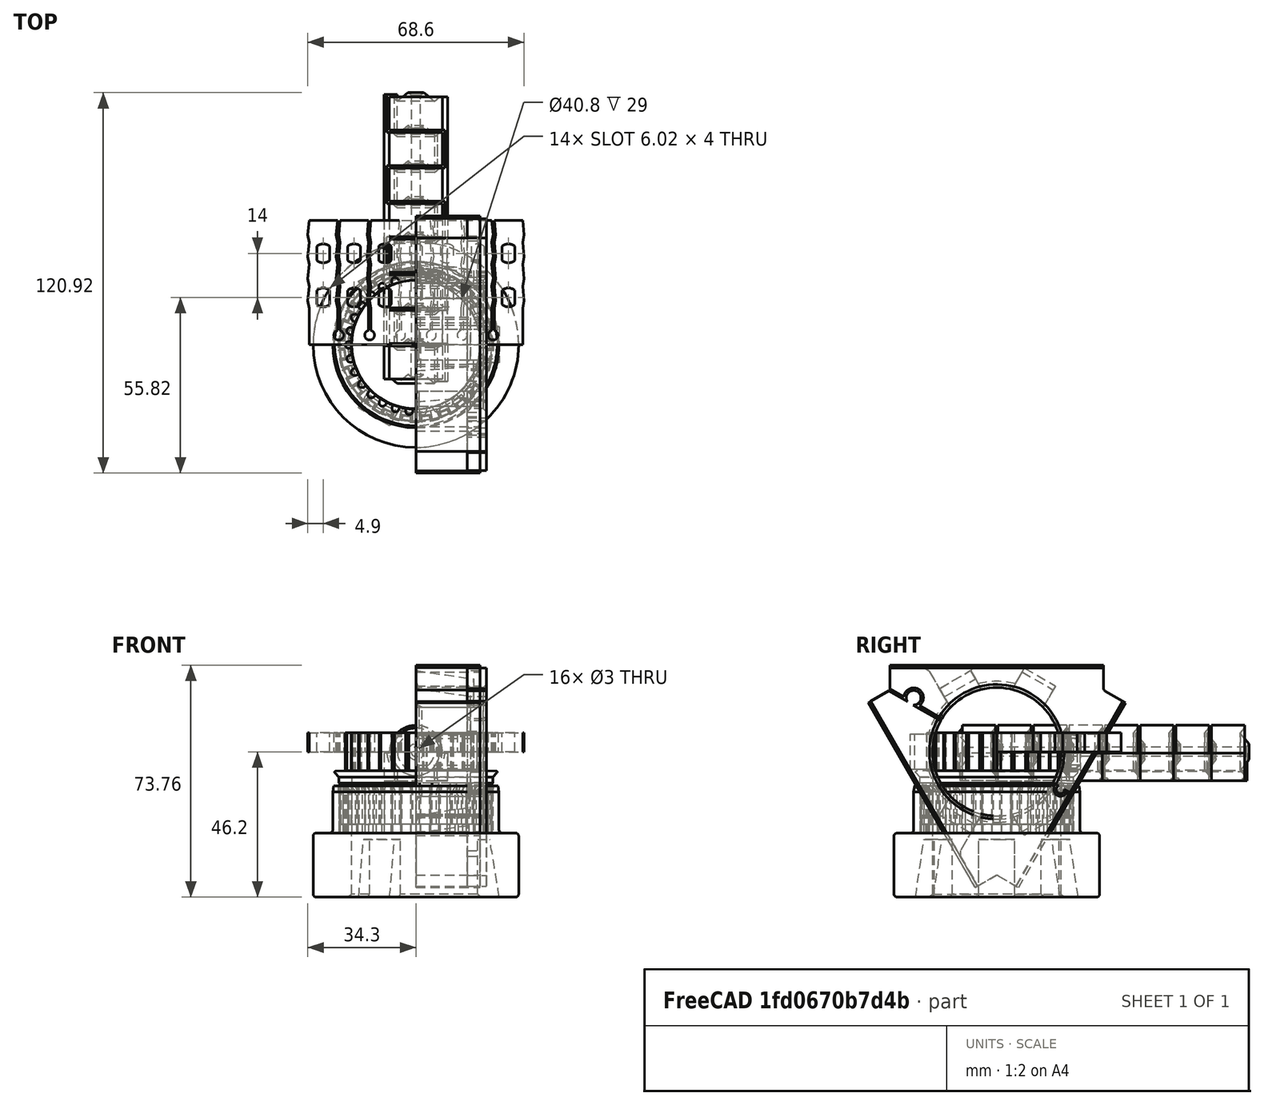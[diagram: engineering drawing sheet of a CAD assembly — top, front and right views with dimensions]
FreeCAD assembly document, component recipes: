
FREECAD ASSEMBLY — COMPONENT RECIPES ("BaseHingeModel_ver1.2_PulleOnAxis")

This assembly document has 9 components, labeled P0..P8 below (a component is one placed body or linked part). 9 of them carry a construction recipe — the FreeCAD feature program that regenerates the part from scratch, quoted from this document or its linked companion documents; the rest are supplied as boundary geometry only. No exploded tour is included for this assembly.
COMPONENT P0 — recipe-attached ("BeamFixatoPart", modeled in this document).
Construction recipe (the document's own serialized feature program — sketch geometry with constraints, then the solid features built on it; lengths are millimeters unless a unit is written):

FEATURE [Sketcher::SketchObject] Sketch022  label="FixatorBodySketch"
  FullyConstrained = false
  MapMode = 5
  Support = -> [XY_Plane005]
  expr: Constraints[143] = Spreadsheet.mmCellWall
  expr: Constraints[144] = Spreadsheet.mmCellWall
  expr: Constraints[145] = Spreadsheet.mmCellWall
  expr: Constraints[146] = Spreadsheet.mmCellWidth
  expr: Constraints[147] = Spreadsheet.mmCellWidth
  expr: Constraints[148] = Spreadsheet.mmCellWidth
  expr: Constraints[169] = Spreadsheet.mmCommonBaseLenght
  expr: Constraints[170] = Spreadsheet.mmToothStep
  expr: Constraints[171] = Spreadsheet.mmToothStep
  expr: Constraints[172] = Spreadsheet.mmToothStep
  expr: Constraints[173] = Spreadsheet.mmToothStep
  expr: Constraints[174] = Spreadsheet.mmToothStep
  expr: Constraints[183] = Spreadsheet.mmCellWall * 3
  expr: Constraints[184] = Spreadsheet.mmCellWall * 3
  expr: Constraints[185] = Spreadsheet.mmCellWall * 3
  expr: Constraints[186] = Spreadsheet.mmCellWall * 3
  expr: Constraints[425] = Spreadsheet.mmFirstCircleArcToBase
  expr: Constraints[435] = Spreadsheet.mmCellWall / 2
  expr: Constraints[464] = Spreadsheet.mmCellWidth + Spreadsheet.mmCellWall
  expr: Constraints[5] = Spreadsheet.mmBaseWidth
  expr: Constraints[6] = Spreadsheet.mmBaseEnd
  sketch-geometry (155):
    g0: LineSegment StartX=-33.9 StartY=0 StartZ=0 EndX=-33.9 EndY=39.5 EndZ=0
    g1: LineSegment StartX=-33.9 StartY=39.5 StartZ=0 EndX=33.9 EndY=39.5 EndZ=0
    g2: LineSegment StartX=33.9 StartY=39.5 StartZ=0 EndX=33.9 EndY=0 EndZ=0
    g3: LineSegment StartX=-73.1099 StartY=25.5 StartZ=0 EndX=65.6354 EndY=25.5 EndZ=0
    g4: LineSegment StartX=-33.9 StartY=0 StartZ=0 EndX=-33.9 EndY=11.5 EndZ=0
    g5: LineSegment StartX=-33.9 StartY=11.5 StartZ=0 EndX=-34.3 EndY=13.9 EndZ=0
    g6: LineSegment StartX=-34.3 StartY=13.9 StartZ=0 EndX=-33.9 EndY=18.5 EndZ=0
    g7: LineSegment StartX=-33.9 StartY=18.5 StartZ=0 EndX=-34.3 EndY=20.9 EndZ=0
    g8: LineSegment StartX=-34.3 StartY=20.9 StartZ=0 EndX=-33.9 EndY=25.5 EndZ=0
    g9: LineSegment StartX=-33.9 StartY=25.5 StartZ=0 EndX=-34.3 EndY=27.9 EndZ=0
    g10: LineSegment StartX=-34.3 StartY=27.9 StartZ=0 EndX=-33.9 EndY=32.5 EndZ=0
    g11: LineSegment StartX=-33.9 StartY=32.5 StartZ=0 EndX=-34.3 EndY=34.9 EndZ=0
    g12: LineSegment StartX=-34.3 StartY=34.9 StartZ=0 EndX=-33.9 EndY=39.5 EndZ=0
    g13: LineSegment StartX=-33.9 StartY=39.5 StartZ=0 EndX=-24.9 EndY=39.5 EndZ=0
    g14: LineSegment StartX=-24.9 StartY=39.5 StartZ=0 EndX=-25.3 EndY=34.9 EndZ=0
    g15: LineSegment StartX=-25.3 StartY=34.9 StartZ=0 EndX=-24.9 EndY=32.5 EndZ=0
    g16: LineSegment StartX=-24.9 StartY=32.5 StartZ=0 EndX=-25.3 EndY=27.9 EndZ=0
    g17: LineSegment StartX=-25.3 StartY=27.9 StartZ=0 EndX=-24.9 EndY=25.5 EndZ=0
    g18: LineSegment StartX=-24.9 StartY=25.5 StartZ=0 EndX=-25.3 EndY=20.9 EndZ=0
    g19: LineSegment StartX=-25.3 StartY=20.9 StartZ=0 EndX=-24.9 EndY=18.5 EndZ=0
    g20: LineSegment StartX=-24.9 StartY=18.5 StartZ=0 EndX=-25.3 EndY=13.9 EndZ=0
    g21: LineSegment StartX=-25.3 StartY=13.9 StartZ=0 EndX=-24.9 EndY=11.5 EndZ=0
    g22: LineSegment StartX=-24.9 StartY=11.5 StartZ=0 EndX=-24.9 EndY=4.5 EndZ=0
    g23: LineSegment StartX=-24.1 StartY=4.5 StartZ=0 EndX=-24.1 EndY=11.5 EndZ=0
    g24: LineSegment StartX=-24.1 StartY=11.5 StartZ=0 EndX=-24.5 EndY=13.9 EndZ=0
    g25: LineSegment StartX=-24.5 StartY=13.9 StartZ=0 EndX=-24.1 EndY=18.5 EndZ=0
    g26: LineSegment StartX=-24.1 StartY=18.5 StartZ=0 EndX=-24.5 EndY=20.9 EndZ=0
    g27: LineSegment StartX=-24.5 StartY=20.9 StartZ=0 EndX=-24.1 EndY=25.5 EndZ=0
    g28: LineSegment StartX=-24.1 StartY=25.5 StartZ=0 EndX=-24.5 EndY=27.9 EndZ=0
    g29: LineSegment StartX=-24.5 StartY=27.9 StartZ=0 EndX=-24.1 EndY=32.5 EndZ=0
    g30: LineSegment StartX=-24.1 StartY=32.5 StartZ=0 EndX=-24.5 EndY=34.9 EndZ=0
    g31: LineSegment StartX=-24.5 StartY=34.9 StartZ=0 EndX=-24.1 EndY=39.5 EndZ=0
    g32: LineSegment StartX=-24.1 StartY=39.5 StartZ=0 EndX=-15.1 EndY=39.5 EndZ=0
    g33: LineSegment StartX=-15.1 StartY=39.5 StartZ=0 EndX=-15.5 EndY=34.9 EndZ=0
    g34: LineSegment StartX=-15.5 StartY=34.9 StartZ=0 EndX=-15.1 EndY=32.5 EndZ=0
    g35: LineSegment StartX=-15.1 StartY=32.5 StartZ=0 EndX=-15.5 EndY=27.9 EndZ=0
    g36: LineSegment StartX=-15.5 StartY=27.9 StartZ=0 EndX=-15.1 EndY=25.5 EndZ=0
    g37: LineSegment StartX=-15.1 StartY=25.5 StartZ=0 EndX=-15.5 EndY=20.9 EndZ=0
    g38: LineSegment StartX=-15.5 StartY=20.9 StartZ=0 EndX=-15.1 EndY=18.5 EndZ=0
    g39: LineSegment StartX=-15.1 StartY=18.5 StartZ=0 EndX=-15.5 EndY=13.9 EndZ=0
    g40: LineSegment StartX=-15.5 StartY=13.9 StartZ=0 EndX=-15.1 EndY=11.5 EndZ=0
    g41: LineSegment StartX=-15.1 StartY=11.5 StartZ=0 EndX=-15.1 EndY=4.5 EndZ=0
    g42: LineSegment StartX=-14.3 StartY=4.5 StartZ=0 EndX=-14.3 EndY=11.5 EndZ=0
    g43: LineSegment StartX=-14.3 StartY=11.5 StartZ=0 EndX=-14.7 EndY=13.9 EndZ=0
    g44: LineSegment StartX=-14.7 StartY=13.9 StartZ=0 EndX=-14.3 EndY=18.5 EndZ=0
    g45: LineSegment StartX=-14.3 StartY=18.5 StartZ=0 EndX=-14.7 EndY=20.9 EndZ=0
    g46: LineSegment StartX=-14.7 StartY=20.9 StartZ=0 EndX=-14.3 EndY=25.5 EndZ=0
    g47: LineSegment StartX=-14.3 StartY=25.5 StartZ=0 EndX=-14.7 EndY=27.9 EndZ=0
    g48: LineSegment StartX=-14.7 StartY=27.9 StartZ=0 EndX=-14.3 EndY=32.5 EndZ=0
    g49: LineSegment StartX=-14.3 StartY=32.5 StartZ=0 EndX=-14.7 EndY=34.9 EndZ=0
    g50: LineSegment StartX=-14.7 StartY=34.9 StartZ=0 EndX=-14.3 EndY=39.5 EndZ=0
    g51: LineSegment StartX=-14.3 StartY=39.5 StartZ=0 EndX=-5.3 EndY=39.5 EndZ=0
    g52: LineSegment StartX=-5.3 StartY=39.5 StartZ=0 EndX=-5.7 EndY=34.9 EndZ=0
    g53: LineSegment StartX=-5.7 StartY=34.9 StartZ=0 EndX=-5.3 EndY=32.5 EndZ=0
    g54: LineSegment StartX=-5.3 StartY=32.5 StartZ=0 EndX=-5.7 EndY=27.9 EndZ=0
    g55: LineSegment StartX=-5.7 StartY=27.9 StartZ=0 EndX=-5.3 EndY=25.5 EndZ=0
    g56: LineSegment StartX=-5.3 StartY=25.5 StartZ=0 EndX=-5.7 EndY=20.9 EndZ=0
    g57: LineSegment StartX=-5.7 StartY=20.9 StartZ=0 EndX=-5.3 EndY=18.5 EndZ=0
    g58: LineSegment StartX=-5.3 StartY=18.5 StartZ=0 EndX=-5.7 EndY=13.9 EndZ=0
    g59: LineSegment StartX=-5.7 StartY=13.9 StartZ=0 EndX=-5.3 EndY=11.5 EndZ=0
    g60: LineSegment StartX=-5.3 StartY=11.5 StartZ=0 EndX=-5.3 EndY=4.5 EndZ=0
    g61: LineSegment StartX=-4.5 StartY=4.5 StartZ=0 EndX=-4.5 EndY=11.5 EndZ=0
    g62: LineSegment StartX=-4.5 StartY=11.5 StartZ=0 EndX=-4.9 EndY=13.9 EndZ=0
    g63: LineSegment StartX=-4.9 StartY=13.9 StartZ=0 EndX=-4.5 EndY=18.5 EndZ=0
    g64: LineSegment StartX=-4.5 StartY=18.5 StartZ=0 EndX=-4.9 EndY=20.9 EndZ=0
    g65: LineSegment StartX=-4.9 StartY=20.9 StartZ=0 EndX=-4.5 EndY=25.5 EndZ=0
    g66: LineSegment StartX=-4.5 StartY=25.5 StartZ=0 EndX=-4.9 EndY=27.9 EndZ=0
    g67: LineSegment StartX=-4.9 StartY=27.9 StartZ=0 EndX=-4.5 EndY=32.5 EndZ=0
    g68: LineSegment StartX=-4.5 StartY=32.5 StartZ=0 EndX=-4.9 EndY=34.9 EndZ=0
    g69: LineSegment StartX=-4.9 StartY=34.9 StartZ=0 EndX=-4.5 EndY=39.5 EndZ=0
    g70: LineSegment StartX=-4.5 StartY=39.5 StartZ=0 EndX=4.5 EndY=39.5 EndZ=0
    g71: LineSegment StartX=4.5 StartY=39.5 StartZ=0 EndX=4.9 EndY=34.9 EndZ=0
    g72: LineSegment StartX=4.9 StartY=34.9 StartZ=0 EndX=4.5 EndY=32.5 EndZ=0
    g73: LineSegment StartX=4.5 StartY=32.5 StartZ=0 EndX=4.9 EndY=27.9 EndZ=0
    g74: LineSegment StartX=4.9 StartY=27.9 StartZ=0 EndX=4.5 EndY=25.5 EndZ=0
    g75: LineSegment StartX=4.5 StartY=25.5 StartZ=0 EndX=4.9 EndY=20.9 EndZ=0
    g76: LineSegment StartX=4.9 StartY=20.9 StartZ=0 EndX=4.5 EndY=18.5 EndZ=0
    g77: LineSegment StartX=4.5 StartY=18.5 StartZ=0 EndX=4.9 EndY=13.9 EndZ=0
    g78: LineSegment StartX=4.9 StartY=13.9 StartZ=0 EndX=4.5 EndY=11.5 EndZ=0
    g79: LineSegment StartX=4.5 StartY=11.5 StartZ=0 EndX=4.5 EndY=4.5 EndZ=0
    g80: LineSegment StartX=5.3 StartY=4.5 StartZ=0 EndX=5.3 EndY=11.5 EndZ=0
    g81: LineSegment StartX=5.3 StartY=11.5 StartZ=0 EndX=5.7 EndY=13.9 EndZ=0
    g82: LineSegment StartX=5.7 StartY=13.9 StartZ=0 EndX=5.3 EndY=18.5 EndZ=0
    g83: LineSegment StartX=5.3 StartY=18.5 StartZ=0 EndX=5.7 EndY=20.9 EndZ=0
    g84: LineSegment StartX=5.7 StartY=20.9 StartZ=0 EndX=5.3 EndY=25.5 EndZ=0
    g85: LineSegment StartX=5.3 StartY=25.5 StartZ=0 EndX=5.7 EndY=27.9 EndZ=0
    g86: LineSegment StartX=5.7 StartY=27.9 StartZ=0 EndX=5.3 EndY=32.5 EndZ=0
    g87: LineSegment StartX=5.3 StartY=32.5 StartZ=0 EndX=5.7 EndY=34.9 EndZ=0
    g88: LineSegment StartX=5.7 StartY=34.9 StartZ=0 EndX=5.3 EndY=39.5 EndZ=0
    g89: LineSegment StartX=5.3 StartY=39.5 StartZ=0 EndX=14.3 EndY=39.5 EndZ=0
    g90: LineSegment StartX=14.3 StartY=39.5 StartZ=0 EndX=14.7 EndY=34.9 EndZ=0
    g91: LineSegment StartX=14.7 StartY=34.9 StartZ=0 EndX=14.3 EndY=32.5 EndZ=0
    g92: LineSegment StartX=14.3 StartY=32.5 StartZ=0 EndX=14.7 EndY=27.9 EndZ=0
    g93: LineSegment StartX=14.7 StartY=27.9 StartZ=0 EndX=14.3 EndY=25.5 EndZ=0
    g94: LineSegment StartX=14.3 StartY=25.5 StartZ=0 EndX=14.7 EndY=20.9 EndZ=0
    g95: LineSegment StartX=14.7 StartY=20.9 StartZ=0 EndX=14.3 EndY=18.5 EndZ=0
    g96: LineSegment StartX=14.3 StartY=18.5 StartZ=0 EndX=14.7 EndY=13.9 EndZ=0
    g97: LineSegment StartX=14.7 StartY=13.9 StartZ=0 EndX=14.3 EndY=11.5 EndZ=0
    g98: LineSegment StartX=14.3 StartY=11.5 StartZ=0 EndX=14.3 EndY=4.5 EndZ=0
    g99: LineSegment StartX=15.1 StartY=4.5 StartZ=0 EndX=15.1 EndY=11.5 EndZ=0
    g100: LineSegment StartX=15.1 StartY=11.5 StartZ=0 EndX=15.5 EndY=13.9 EndZ=0
    g101: LineSegment StartX=15.5 StartY=13.9 StartZ=0 EndX=15.1 EndY=18.5 EndZ=0
    g102: LineSegment StartX=15.1 StartY=18.5 StartZ=0 EndX=15.5 EndY=20.9 EndZ=0
    g103: LineSegment StartX=15.5 StartY=20.9 StartZ=0 EndX=15.1 EndY=25.5 EndZ=0
    g104: LineSegment StartX=15.1 StartY=25.5 StartZ=0 EndX=15.5 EndY=27.9 EndZ=0
    g105: LineSegment StartX=15.5 StartY=27.9 StartZ=0 EndX=15.1 EndY=32.5 EndZ=0
    g106: LineSegment StartX=15.1 StartY=32.5 StartZ=0 EndX=15.5 EndY=34.9 EndZ=0
    g107: LineSegment StartX=15.5 StartY=34.9 StartZ=0 EndX=15.1 EndY=39.5 EndZ=0
    g108: LineSegment StartX=15.1 StartY=39.5 StartZ=0 EndX=24.1 EndY=39.5 EndZ=0
    g109: LineSegment StartX=24.1 StartY=39.5 StartZ=0 EndX=24.5 EndY=34.9 EndZ=0
    g110: LineSegment StartX=24.5 StartY=34.9 StartZ=0 EndX=24.1 EndY=32.5 EndZ=0
    g111: LineSegment StartX=24.1 StartY=32.5 StartZ=0 EndX=24.5 EndY=27.9 EndZ=0
    g112: LineSegment StartX=24.5 StartY=27.9 StartZ=0 EndX=24.1 EndY=25.5 EndZ=0
    g113: LineSegment StartX=24.1 StartY=25.5 StartZ=0 EndX=24.5 EndY=20.9 EndZ=0
    g114: LineSegment StartX=24.5 StartY=20.9 StartZ=0 EndX=24.1 EndY=18.5 EndZ=0
    g115: LineSegment StartX=24.1 StartY=18.5 StartZ=0 EndX=24.5 EndY=13.9 EndZ=0
    g116: LineSegment StartX=24.5 StartY=13.9 StartZ=0 EndX=24.1 EndY=11.5 EndZ=0
    g117: LineSegment StartX=24.1 StartY=11.5 StartZ=0 EndX=24.1 EndY=4.5 EndZ=0
    g118: LineSegment StartX=24.9 StartY=4.5 StartZ=0 EndX=24.9 EndY=11.5 EndZ=0
    g119: LineSegment StartX=24.9 StartY=11.5 StartZ=0 EndX=25.3 EndY=13.9 EndZ=0
    g120: LineSegment StartX=25.3 StartY=13.9 StartZ=0 EndX=24.9 EndY=18.5 EndZ=0
    g121: LineSegment StartX=24.9 StartY=18.5 StartZ=0 EndX=25.3 EndY=20.9 EndZ=0
    g122: LineSegment StartX=25.3 StartY=20.9 StartZ=0 EndX=24.9 EndY=25.5 EndZ=0
    g123: LineSegment StartX=24.9 StartY=25.5 StartZ=0 EndX=25.3 EndY=27.9 EndZ=0
    g124: LineSegment StartX=25.3 StartY=27.9 StartZ=0 EndX=24.9 EndY=32.5 EndZ=0
    g125: LineSegment StartX=24.9 StartY=32.5 StartZ=0 EndX=25.3 EndY=34.9 EndZ=0
    g126: LineSegment StartX=25.3 StartY=34.9 StartZ=0 EndX=24.9 EndY=39.5 EndZ=0
    g127: LineSegment StartX=24.9 StartY=39.5 StartZ=0 EndX=33.9 EndY=39.5 EndZ=0
    g128: LineSegment StartX=33.9 StartY=39.5 StartZ=0 EndX=34.3 EndY=34.9 EndZ=0
    g129: LineSegment StartX=34.3 StartY=34.9 StartZ=0 EndX=33.9 EndY=32.5 EndZ=0
    g130: LineSegment StartX=33.9 StartY=32.5 StartZ=0 EndX=34.3 EndY=27.9 EndZ=0
    g131: LineSegment StartX=34.3 StartY=27.9 StartZ=0 EndX=33.9 EndY=25.5 EndZ=0
    g132: LineSegment StartX=33.9 StartY=25.5 StartZ=0 EndX=34.3 EndY=20.9 EndZ=0
    g133: LineSegment StartX=34.3 StartY=20.9 StartZ=0 EndX=33.9 EndY=18.5 EndZ=0
    g134: LineSegment StartX=33.9 StartY=18.5 StartZ=0 EndX=34.3 EndY=13.9 EndZ=0
    g135: LineSegment StartX=34.3 StartY=13.9 StartZ=0 EndX=33.9 EndY=11.5 EndZ=0
    g136: LineSegment StartX=33.9 StartY=11.5 StartZ=0 EndX=33.9 EndY=0 EndZ=0
    g137: LineSegment StartX=33.9 StartY=0 StartZ=0 EndX=-33.9 EndY=0 EndZ=0
    g138: LineSegment StartX=-73.1099 StartY=18.5 StartZ=0 EndX=65.6354 EndY=18.5 EndZ=0
    g139: LineSegment StartX=-73.1099 StartY=34.9 StartZ=0 EndX=65.6354 EndY=34.9 EndZ=0
    g140: LineSegment StartX=-73.1099 StartY=32.5 StartZ=0 EndX=65.6354 EndY=32.5 EndZ=0
    g141: LineSegment StartX=-73.1099 StartY=27.9 StartZ=0 EndX=65.6354 EndY=27.9 EndZ=0
    g142: LineSegment StartX=-73.1099 StartY=20.9 StartZ=0 EndX=65.6354 EndY=20.9 EndZ=0
    g143: LineSegment StartX=-73.1099 StartY=11.5 StartZ=0 EndX=65.6354 EndY=11.5 EndZ=0
    g144: LineSegment StartX=-34.3 StartY=8.59208 StartZ=0 EndX=-34.3 EndY=49.4346 EndZ=0
    g145: LineSegment StartX=-73.1099 StartY=13.9 StartZ=0 EndX=65.6354 EndY=13.9 EndZ=0
    g146: LineSegment StartX=-33.9 StartY=0 StartZ=0 EndX=33.9 EndY=0 EndZ=0
    g147: LineSegment StartX=-73.1099 StartY=4.5 StartZ=0 EndX=65.6354 EndY=4.5 EndZ=0
    g148: ArcOfCircle CenterX=-24.5 CenterY=3 CenterZ=0 NormalX=0 NormalY=0 NormalZ=1 AngleXU=0 Radius=1.55242 StartAngle=1.8314 EndAngle=7.59338
    g149: ArcOfCircle CenterX=-14.7 CenterY=3 CenterZ=0 NormalX=0 NormalY=0 NormalZ=1 AngleXU=0 Radius=1.55242 StartAngle=1.8314 EndAngle=7.59338
    g150: ArcOfCircle CenterX=-4.9 CenterY=3 CenterZ=0 NormalX=0 NormalY=0 NormalZ=1 AngleXU=0 Radius=1.55242 StartAngle=1.8314 EndAngle=7.59338
    g151: ArcOfCircle CenterX=4.9 CenterY=3 CenterZ=0 NormalX=0 NormalY=0 NormalZ=1 AngleXU=0 Radius=1.55242 StartAngle=1.8314 EndAngle=7.59338
    g152: ArcOfCircle CenterX=14.7 CenterY=3 CenterZ=0 NormalX=0 NormalY=0 NormalZ=1 AngleXU=0 Radius=1.55242 StartAngle=1.8314 EndAngle=7.59338
    g153: ArcOfCircle CenterX=24.5 CenterY=3 CenterZ=0 NormalX=0 NormalY=0 NormalZ=1 AngleXU=0 Radius=1.55242 StartAngle=1.8314 EndAngle=7.59338
    g154: LineSegment StartX=-73.1099 StartY=3 StartZ=0 EndX=65.6354 EndY=3 EndZ=0
  constraints (469):
    c: Coincident(g0,g1)
    c: Coincident(g1,g2)
    c: Horizontal(g3)
    c: Symmetric(g0,g2,g-2)
    c: Symmetric(g1,g0,g-2)
    c: DistanceX(g0,g2) = 67.8
    c: DistanceX(g0,g1) = 67.8
    c: Coincident(g4,g5)
    c: Coincident(g5,g6)
    c: Coincident(g6,g7)
    c: Coincident(g7,g8)
    c: Coincident(g8,g9)
    c: Coincident(g9,g10)
    c: Coincident(g10,g11)
    c: Coincident(g11,g12)
    c: Coincident(g12,g13)
    c: Horizontal(g13)
    c: Coincident(g13,g14)
    c: Coincident(g14,g15)
    c: Coincident(g15,g16)
    c: Coincident(g16,g17)
    c: Coincident(g17,g18)
    c: Coincident(g18,g19)
    c: Coincident(g19,g20)
    c: Coincident(g20,g21)
    c: Coincident(g21,g22)
    c: Coincident(g23,g24)
    c: Coincident(g24,g25)
    c: Coincident(g25,g26)
    c: Coincident(g26,g27)
    c: Coincident(g27,g28)
    c: Coincident(g28,g29)
    c: Coincident(g29,g30)
    c: Coincident(g30,g31)
    c: Coincident(g31,g32)
    c: Horizontal(g32)
    c: Coincident(g32,g33)
    c: Coincident(g33,g34)
    c: Coincident(g34,g35)
    c: Coincident(g35,g36)
    c: Coincident(g36,g37)
    c: Coincident(g37,g38)
    c: Coincident(g38,g39)
    c: Coincident(g39,g40)
    c: Coincident(g40,g41)
    c: Coincident(g42,g43)
    c: Coincident(g43,g44)
    c: Coincident(g44,g45)
    c: Coincident(g45,g46)
    c: Coincident(g46,g47)
    c: Coincident(g47,g48)
    c: Coincident(g48,g49)
    c: Coincident(g49,g50)
    c: Coincident(g50,g51)
    c: Coincident(g51,g52)
    c: Coincident(g52,g53)
    c: Coincident(g53,g54)
    c: Coincident(g54,g55)
    c: Coincident(g55,g56)
    c: Coincident(g56,g57)
    c: Coincident(g57,g58)
    c: Coincident(g58,g59)
    c: Coincident(g59,g60)
    c: Coincident(g61,g62)
    c: Coincident(g62,g63)
    c: Coincident(g63,g64)
    c: Coincident(g64,g65)
    c: Coincident(g65,g66)
    c: Coincident(g66,g67)
    c: Coincident(g67,g68)
    c: Coincident(g68,g69)
    c: Coincident(g69,g70)
    c: Coincident(g70,g71)
    c: Coincident(g71,g72)
    c: Coincident(g72,g73)
    c: Coincident(g73,g74)
    c: Coincident(g74,g75)
    c: Coincident(g75,g76)
    c: Coincident(g76,g77)
    c: Coincident(g77,g78)
    c: Coincident(g78,g79)
    c: Coincident(g80,g81)
    c: Coincident(g81,g82)
    c: Coincident(g82,g83)
    c: Coincident(g83,g84)
    c: Coincident(g84,g85)
    c: Coincident(g85,g86)
    c: Coincident(g86,g87)
    c: Coincident(g87,g88)
    c: Coincident(g88,g89)
    c: Horizontal(g89)
    c: Coincident(g89,g90)
    c: Coincident(g90,g91)
    c: Coincident(g91,g92)
    c: Coincident(g92,g93)
    c: Coincident(g93,g94)
    c: Coincident(g94,g95)
    c: Coincident(g95,g96)
    c: Coincident(g96,g97)
    c: Coincident(g97,g98)
    c: Coincident(g99,g100)
    c: Coincident(g100,g101)
    c: Coincident(g101,g102)
    c: Coincident(g102,g103)
    c: Coincident(g103,g104)
    c: Coincident(g104,g105)
    c: Coincident(g105,g106)
    c: Coincident(g106,g107)
    c: Coincident(g107,g108)
    c: Coincident(g108,g109)
    c: Coincident(g109,g110)
    c: Coincident(g110,g111)
    c: Coincident(g111,g112)
    c: Coincident(g112,g113)
    c: Coincident(g113,g114)
    c: Coincident(g114,g115)
    c: Coincident(g115,g116)
    c: Coincident(g116,g117)
    c: Coincident(g118,g119)
    c: Coincident(g119,g120)
    c: Coincident(g120,g121)
    c: Coincident(g121,g122)
    c: Coincident(g122,g123)
    c: Coincident(g123,g124)
    c: Coincident(g124,g125)
    c: Coincident(g125,g126)
    c: Coincident(g126,g127)
    c: Coincident(g127,g128)
    c: Coincident(g128,g129)
    c: Coincident(g129,g130)
    c: Coincident(g130,g131)
    c: Coincident(g131,g132)
    c: Coincident(g132,g133)
    c: Coincident(g133,g134)
    c: Coincident(g134,g135)
    c: Coincident(g135,g136)
    c: Symmetric(g69,g70,g-2)
    c: Symmetric(g51,g88,g-2)
    c: Symmetric(g50,g89,g-2)
    c: Symmetric(g32,g107,g-2)
    c: Symmetric(g31,g108,g-2)
    c: Symmetric(g13,g126,g-2)
    c: Symmetric(g12,g127,g-2)
    c: DistanceX(g13,g31) = 0.8
    c: DistanceX(g32,g50) = 0.8
    c: DistanceX(g51,g69) = 0.8
    c: DistanceX(g13,g13) = 9
    c: DistanceX(g32,g32) = 9
    c: DistanceX(g51,g51) = 9
    c: Horizontal(g139)
    c: Horizontal(g140)
    c: Horizontal(g141)
    c: Horizontal(g142)
    c: Horizontal(g143)
    c: Vertical(g8,g6)
    c: Vertical(g6,g4)
    c: Vertical(g144)
    c: Horizontal(g145)
    c: Coincident(g146,g0)
    c: Coincident(g146,g2)
    c: Coincident(g0,g137)
    c: Coincident(g2,g137)
    c: Horizontal(g147)
    c: PointOnObject(g11,g139)
    c: PointOnObject(g11,g144)
    c: PointOnObject(g10,g140)
    c: PointOnObject(g9,g144)
    c: PointOnObject(g7,g142)
    c: Horizontal(g138)
    c: DistanceY(g137,g147) = 4.5
    c: DistanceY(g147,g143) = 7
    c: DistanceY(g143,g138) = 7
    c: DistanceY(g138,g3) = 7
    c: DistanceY(g3,g140) = 7
    c: DistanceY(g140,g0) = 7
    c: Vertical(g139,g140)
    c: Vertical(g140,g141)
    c: Vertical(g141,g3)
    c: Vertical(g3,g142)
    c: Vertical(g142,g138)
    c: Vertical(g138,g145)
    c: Vertical(g145,g143)
    c: Vertical(g143,g147)
    c: DistanceY(g143,g145) = 2.4
    c: DistanceY(g138,g142) = 2.4
    c: DistanceY(g3,g141) = 2.4
    c: DistanceY(g140,g139) = 2.4
    c: Parallel(g12,g14)
    c: Parallel(g11,g15)
    c: PointOnObject(g14,g139)
    c: PointOnObject(g30,g139)
    c: PointOnObject(g15,g140)
    c: PointOnObject(g29,g140)
    c: Parallel(g14,g31)
    c: PointOnObject(g16,g141)
    c: PointOnObject(g28,g141)
    c: PointOnObject(g17,g3)
    c: PointOnObject(g27,g3)
    c: PointOnObject(g18,g142)
    c: PointOnObject(g26,g142)
    c: PointOnObject(g19,g138)
    c: PointOnObject(g25,g138)
    c: PointOnObject(g20,g145)
    c: PointOnObject(g24,g145)
    c: PointOnObject(g21,g143)
    c: PointOnObject(g23,g143)
    c: PointOnObject(g22,g147)
    c: PointOnObject(g23,g147)
    c: PointOnObject(g33,g139)
    c: PointOnObject(g49,g139)
    c: PointOnObject(g52,g139)
    c: PointOnObject(g71,g139)
    c: PointOnObject(g87,g139)
    c: PointOnObject(g90,g139)
    c: PointOnObject(g106,g139)
    c: PointOnObject(g109,g139)
    c: PointOnObject(g125,g139)
    c: PointOnObject(g128,g139)
    c: PointOnObject(g34,g140)
    c: PointOnObject(g48,g140)
    c: PointOnObject(g53,g140)
    c: PointOnObject(g67,g140)
    c: PointOnObject(g72,g140)
    c: PointOnObject(g86,g140)
    c: PointOnObject(g91,g140)
    c: PointOnObject(g105,g140)
    c: PointOnObject(g110,g140)
    c: PointOnObject(g124,g140)
    c: PointOnObject(g129,g140)
    c: Parallel(g33,g50)
    c: Parallel(g52,g69)
    c: Parallel(g71,g88)
    c: Parallel(g71,g90)
    c: Parallel(g90,g107)
    c: Parallel(g71,g109)
    c: Parallel(g109,g126)
    c: Parallel(g126,g128)
    c: Symmetric(g71,g68,g-2)
    c: Symmetric(g72,g67,g-2)
    c: Vertical(g139,g140)
    c: Vertical(g140,g141)
    c: Vertical(g141,g3)
    c: Vertical(g3,g142)
    c: Vertical(g142,g138)
    c: Vertical(g138,g145)
    c: Vertical(g145,g143)
    c: Vertical(g143,g147)
    c: Parallel(g34,g49)
    c: Parallel(g49,g53)
    c: Parallel(g53,g68)
    c: Parallel(g35,g48)
    c: Parallel(g48,g54)
    c: Parallel(g54,g67)
    c: PointOnObject(g35,g141)
    c: PointOnObject(g47,g141)
    c: PointOnObject(g54,g141)
    c: PointOnObject(g66,g141)
    c: PointOnObject(g85,g141)
    c: PointOnObject(g92,g141)
    c: PointOnObject(g104,g141)
    c: PointOnObject(g111,g141)
    c: PointOnObject(g123,g141)
    c: PointOnObject(g130,g141)
    c: Symmetric(g66,g73,g-2)
    c: Symmetric(g65,g74,g-2)
    c: PointOnObject(g36,g3)
    c: PointOnObject(g46,g3)
    c: PointOnObject(g55,g3)
    c: PointOnObject(g65,g3)
    c: Parallel(g36,g47)
    c: Parallel(g47,g55)
    c: Parallel(g55,g66)
    c: Symmetric(g64,g75,g-2)
    c: Symmetric(g79,g61,g-2)
    c: Symmetric(g61,g78,g-2)
    c: Symmetric(g62,g77,g-2)
    c: Symmetric(g63,g76,g-2)
    c: Parallel(g37,g46)
    c: Parallel(g46,g56)
    c: Parallel(g56,g65)
    c: PointOnObject(g37,g142)
    c: PointOnObject(g45,g142)
    c: PointOnObject(g56,g142)
    c: PointOnObject(g64,g142)
    c: PointOnObject(g38,g138)
    c: PointOnObject(g44,g138)
    c: PointOnObject(g57,g138)
    c: PointOnObject(g63,g138)
    c: Parallel(g38,g45)
    c: Parallel(g45,g57)
    c: Parallel(g57,g64)
    c: PointOnObject(g39,g145)
    c: PointOnObject(g43,g145)
    c: PointOnObject(g58,g145)
    c: PointOnObject(g62,g145)
    c: Parallel(g39,g44)
    c: Parallel(g44,g58)
    c: Parallel(g58,g63)
    c: Parallel(g40,g43)
    c: Parallel(g43,g59)
    c: Parallel(g59,g62)
    c: PointOnObject(g40,g143)
    c: PointOnObject(g42,g143)
    c: PointOnObject(g59,g143)
    c: PointOnObject(g61,g143)
    c: PointOnObject(g41,g147)
    c: PointOnObject(g42,g147)
    c: PointOnObject(g60,g147)
    c: PointOnObject(g61,g147)
    c: Parallel(g41,g42)
    c: Parallel(g42,g60)
    c: Parallel(g60,g61)
    c: PointOnObject(g80,g147)
    c: PointOnObject(g98,g147)
    c: PointOnObject(g99,g147)
    c: PointOnObject(g117,g147)
    c: PointOnObject(g118,g147)
    c: PointOnObject(g80,g143)
    c: PointOnObject(g97,g143)
    c: PointOnObject(g99,g143)
    c: PointOnObject(g116,g143)
    c: PointOnObject(g118,g143)
    c: PointOnObject(g135,g143)
    c: Parallel(g79,g80)
    c: Parallel(g80,g98)
    c: Parallel(g98,g99)
    c: Parallel(g99,g117)
    c: Parallel(g117,g118)
    c: Parallel(g118,g136)
    c: Parallel(g72,g87)
    c: Parallel(g87,g91)
    c: Parallel(g91,g106)
    c: Parallel(g106,g110)
    c: Parallel(g110,g125)
    c: Parallel(g125,g129)
    c: Parallel(g73,g86)
    c: Parallel(g86,g92)
    c: Parallel(g92,g105)
    c: Parallel(g105,g111)
    c: Parallel(g111,g124)
    c: Parallel(g124,g130)
    c: PointOnObject(g84,g3)
    c: PointOnObject(g93,g3)
    c: PointOnObject(g103,g3)
    c: PointOnObject(g112,g3)
    c: PointOnObject(g122,g3)
    c: PointOnObject(g131,g3)
    c: Parallel(g74,g85)
    c: Parallel(g85,g93)
    c: Parallel(g93,g104)
    c: Parallel(g104,g112)
    c: Parallel(g112,g123)
    c: Parallel(g123,g131)
    c: PointOnObject(g83,g142)
    c: PointOnObject(g94,g142)
    c: PointOnObject(g102,g142)
    c: PointOnObject(g113,g142)
    c: PointOnObject(g121,g142)
    c: PointOnObject(g132,g142)
    c: Parallel(g75,g84)
    c: Parallel(g84,g94)
    c: Parallel(g94,g103)
    c: Parallel(g103,g113)
    c: Parallel(g113,g122)
    c: Parallel(g122,g132)
    c: PointOnObject(g82,g138)
    c: PointOnObject(g95,g138)
    c: PointOnObject(g101,g138)
    c: PointOnObject(g114,g138)
    c: PointOnObject(g120,g138)
    c: PointOnObject(g133,g138)
    c: PointOnObject(g81,g145)
    c: PointOnObject(g96,g145)
    c: PointOnObject(g100,g145)
    c: PointOnObject(g115,g145)
    c: PointOnObject(g119,g145)
    c: PointOnObject(g134,g145)
    c: Parallel(g76,g83)
    c: Parallel(g83,g95)
    c: Parallel(g95,g102)
    c: Parallel(g102,g114)
    c: Parallel(g114,g121)
    c: Parallel(g121,g133)
    c: Parallel(g77,g82)
    c: Parallel(g82,g96)
    c: Parallel(g96,g101)
    c: Parallel(g101,g115)
    c: Parallel(g115,g120)
    c: Parallel(g120,g134)
    c: Parallel(g78,g81)
    c: Parallel(g81,g97)
    c: Parallel(g97,g100)
    c: Parallel(g100,g116)
    c: Parallel(g116,g119)
    c: Parallel(g119,g135)
    c: DistanceY(g137,g-1) = 0
    c: PointOnObject(g148,g154)
    c: PointOnObject(g149,g154)
    c: PointOnObject(g150,g154)
    c: PointOnObject(g151,g154)
    c: PointOnObject(g152,g154)
    c: PointOnObject(g153,g154)
    c: PointOnObject(g22,g148)
    c: PointOnObject(g23,g148)
    c: PointOnObject(g41,g149)
    c: PointOnObject(g42,g149)
    c: PointOnObject(g60,g150)
    c: PointOnObject(g61,g150)
    c: PointOnObject(g79,g151)
    c: PointOnObject(g98,g152)
    c: PointOnObject(g99,g152)
    c: PointOnObject(g117,g153)
    c: PointOnObject(g118,g153)
    c: PointOnObject(g153,g147)
    c: PointOnObject(g153,g147)
    c: PointOnObject(g152,g147)
    c: PointOnObject(g152,g147)
    c: PointOnObject(g151,g147)
    c: PointOnObject(g151,g147)
    c: PointOnObject(g150,g147)
    c: PointOnObject(g150,g147)
    c: PointOnObject(g149,g147)
    c: PointOnObject(g149,g147)
    c: PointOnObject(g148,g147)
    c: PointOnObject(g148,g147)
    c: DistanceY(g154,g147) = 1.5
    c: Vertical(g147,g154)
    c: Vertical(g147,g154)
    c: Coincident(g136,g137)
    c: Coincident(g4,g137)
    c: Coincident(g0,g12)
    c: PointOnObject(g31,g1)
    c: PointOnObject(g50,g1)
    c: PointOnObject(g69,g1)
    c: PointOnObject(g6,g0)
    c: DistanceX(g144,g12) = 0.4
    c: PointOnObject(g9,g141)
    c: PointOnObject(g8,g3)
    c: PointOnObject(g7,g144)
    c: PointOnObject(g6,g138)
    c: PointOnObject(g5,g145)
    c: PointOnObject(g5,g144)
    c: PointOnObject(g4,g143)
    c: Parallel(g12,g33)
    c: Parallel(g12,g52)
    c: Parallel(g15,g30)
    c: Parallel(g11,g34)
    c: PointOnObject(g10,g0)
    c: Parallel(g16,g29)
    c: Parallel(g10,g16)
    c: Parallel(g10,g35)
    c: Parallel(g9,g17)
    c: Parallel(g17,g28)
    c: Parallel(g9,g36)
    c: Parallel(g18,g27)
    c: Parallel(g8,g18)
    c: Parallel(g8,g37)
    c: Parallel(g7,g19)
    c: Parallel(g19,g26)
    c: Parallel(g6,g20)
    c: Parallel(g20,g25)
    c: Parallel(g7,g38)
    c: Parallel(g6,g39)
    c: Symmetric(g150,g151,g-2)
    c: DistanceX(g150,g151) = 9.8
    c: Parallel(g23,g22)
    c: Parallel(g21,g24)
    c: Parallel(g5,g21)
    c: Parallel(g41,g23)
FEATURE [PartDesign::Pad] Pad  label="FixatorPadBody"
  Direction = (0,0,1)
  Length = 6
  Length2 = 10
  Profile = -> Sketch022
  ReferenceAxis = -> Sketch022 [N_Axis]
  Type = 0
  expr: Length = Spreadsheet.mmCellHight
FEATURE [Sketcher::SketchObject] Sketch  label="PiercesPocketSketch"
  AttachmentOffset = pos=(0,0,0) rot=(1,0,0;1.5708rad)
  FullyConstrained = true
  MapMode = 2
  Placement = pos=(0,0,0) rot=(0.707107,0.707107,0;3.14159rad)
  Support = -> [YZ_Plane005]
  expr: Constraints[108] = Spreadsheet.mmCellPierceWidth
  expr: Constraints[118] = Spreadsheet.mmCellPierceWidth
  expr: Constraints[128] = Spreadsheet.mmCellPierceWidth
  expr: Constraints[138] = Spreadsheet.mmCellPierceWidth
  expr: Constraints[148] = Spreadsheet.mmCellPierceWidth
  expr: Constraints[158] = Spreadsheet.mmCellPierceWidth
  expr: Constraints[171] = Spreadsheet.mmCellWidth + Spreadsheet.mmCellWall
  expr: Constraints[172] = Spreadsheet.mmCellWidth + Spreadsheet.mmCellWall
  expr: Constraints[173] = Spreadsheet.mmCellWidth + Spreadsheet.mmCellWall
  expr: Constraints[174] = Spreadsheet.mmCellWidth + Spreadsheet.mmCellWall
  expr: Constraints[175] = Spreadsheet.mmCellWidth + Spreadsheet.mmCellWall
  expr: Constraints[176] = Spreadsheet.mmCellWidth + Spreadsheet.mmCellWall
  expr: Constraints[178] = Spreadsheet.mmCellWidth / 2
  expr: Constraints[179] = Spreadsheet.mmCellWidth / 2
  expr: Constraints[180] = Spreadsheet.mmCommonBaseLenght + Spreadsheet.mmToothStep * 1.5
  expr: Constraints[181] = Spreadsheet.mmToothStep * 2
  expr: Constraints[19] = Spreadsheet.mmCellPierceWidth
  expr: Constraints[29] = Spreadsheet.mmCellPierceWidth
  expr: Constraints[39] = Spreadsheet.mmCellPierceWidth
  expr: Constraints[49] = Spreadsheet.mmCellPierceWidth
  expr: Constraints[59] = Spreadsheet.mmCellPierceWidth
  expr: Constraints[69] = Spreadsheet.mmCellPierceWidth
  expr: Constraints[82] = Spreadsheet.mmCellWidth + Spreadsheet.mmCellWall
  expr: Constraints[83] = Spreadsheet.mmCellWidth + Spreadsheet.mmCellWall
  expr: Constraints[84] = Spreadsheet.mmCellWidth + Spreadsheet.mmCellWall
  expr: Constraints[85] = Spreadsheet.mmCellWidth + Spreadsheet.mmCellWall
  expr: Constraints[86] = Spreadsheet.mmCellWidth + Spreadsheet.mmCellWall
  expr: Constraints[87] = Spreadsheet.mmCellWidth + Spreadsheet.mmCellWall
  expr: Constraints[98] = Spreadsheet.mmCellPierceWidth
  expr: Constraints[9] = Spreadsheet.mmCellPierceWidth
  sketch-geometry (56):
    g0: ArcOfCircle CenterX=29 CenterY=0 CenterZ=0 NormalX=0 NormalY=0 NormalZ=1 AngleXU=0 Radius=3.0104 StartAngle=2.41495 EndAngle=3.86823
    g1: LineSegment StartX=26.75 StartY=2 StartZ=0 EndX=31.25 EndY=2 EndZ=0
    g2: LineSegment StartX=26.75 StartY=-2 StartZ=0 EndX=31.25 EndY=-2 EndZ=0
    g3: ArcOfCircle CenterX=29 CenterY=0 CenterZ=0 NormalX=0 NormalY=0 NormalZ=1 AngleXU=0 Radius=3.0104 StartAngle=5.55654 EndAngle=7.00983
    g4: ArcOfCircle CenterX=29 CenterY=9.8 CenterZ=0 NormalX=0 NormalY=0 NormalZ=1 AngleXU=0 Radius=3.0104 StartAngle=2.41495 EndAngle=3.86823
    g5: LineSegment StartX=26.75 StartY=11.8 StartZ=0 EndX=31.25 EndY=11.8 EndZ=0
    g6: LineSegment StartX=26.75 StartY=7.8 StartZ=0 EndX=31.25 EndY=7.8 EndZ=0
    g7: ArcOfCircle CenterX=29 CenterY=9.8 CenterZ=0 NormalX=0 NormalY=0 NormalZ=1 AngleXU=0 Radius=3.0104 StartAngle=5.55654 EndAngle=7.00983
    g8: ArcOfCircle CenterX=29 CenterY=19.6 CenterZ=0 NormalX=0 NormalY=0 NormalZ=1 AngleXU=0 Radius=3.0104 StartAngle=2.41495 EndAngle=3.86823
    g9: LineSegment StartX=26.75 StartY=21.6 StartZ=0 EndX=31.25 EndY=21.6 EndZ=0
    g10: LineSegment StartX=26.75 StartY=17.6 StartZ=0 EndX=31.25 EndY=17.6 EndZ=0
    g11: ArcOfCircle CenterX=29 CenterY=19.6 CenterZ=0 NormalX=0 NormalY=0 NormalZ=1 AngleXU=0 Radius=3.0104 StartAngle=5.55654 EndAngle=7.00983
    g12: ArcOfCircle CenterX=29 CenterY=29.4 CenterZ=0 NormalX=0 NormalY=0 NormalZ=1 AngleXU=0 Radius=3.0104 StartAngle=2.41495 EndAngle=3.86823
    g13: LineSegment StartX=26.75 StartY=31.4 StartZ=0 EndX=31.25 EndY=31.4 EndZ=0
    g14: LineSegment StartX=26.75 StartY=27.4 StartZ=0 EndX=31.25 EndY=27.4 EndZ=0
    g15: ArcOfCircle CenterX=29 CenterY=29.4 CenterZ=0 NormalX=0 NormalY=0 NormalZ=1 AngleXU=0 Radius=3.0104 StartAngle=5.55654 EndAngle=7.00983
    g16: ArcOfCircle CenterX=29 CenterY=-9.8 CenterZ=0 NormalX=0 NormalY=0 NormalZ=1 AngleXU=0 Radius=3.0104 StartAngle=2.41495 EndAngle=3.86823
    g17: LineSegment StartX=26.75 StartY=-7.8 StartZ=0 EndX=31.25 EndY=-7.8 EndZ=0
    g18: LineSegment StartX=26.75 StartY=-11.8 StartZ=0 EndX=31.25 EndY=-11.8 EndZ=0
    g19: ArcOfCircle CenterX=29 CenterY=-9.8 CenterZ=0 NormalX=0 NormalY=0 NormalZ=1 AngleXU=0 Radius=3.0104 StartAngle=5.55654 EndAngle=7.00983
    g20: ArcOfCircle CenterX=29 CenterY=-19.6 CenterZ=0 NormalX=0 NormalY=0 NormalZ=1 AngleXU=0 Radius=3.0104 StartAngle=2.41495 EndAngle=3.86823
    g21: LineSegment StartX=26.75 StartY=-17.6 StartZ=0 EndX=31.25 EndY=-17.6 EndZ=0
    g22: LineSegment StartX=26.75 StartY=-21.6 StartZ=0 EndX=31.25 EndY=-21.6 EndZ=0
    g23: ArcOfCircle CenterX=29 CenterY=-19.6 CenterZ=0 NormalX=0 NormalY=0 NormalZ=1 AngleXU=0 Radius=3.0104 StartAngle=5.55654 EndAngle=7.00983
    g24: ArcOfCircle CenterX=29 CenterY=-29.4 CenterZ=0 NormalX=0 NormalY=0 NormalZ=1 AngleXU=0 Radius=3.0104 StartAngle=2.41495 EndAngle=3.86823
    g25: LineSegment StartX=26.75 StartY=-27.4 StartZ=0 EndX=31.25 EndY=-27.4 EndZ=0
    g26: LineSegment StartX=26.75 StartY=-31.4 StartZ=0 EndX=31.25 EndY=-31.4 EndZ=0
    g27: ArcOfCircle CenterX=29 CenterY=-29.4 CenterZ=0 NormalX=0 NormalY=0 NormalZ=1 AngleXU=0 Radius=3.0104 StartAngle=5.55654 EndAngle=7.00983
    g28: ArcOfCircle CenterX=15 CenterY=0 CenterZ=0 NormalX=0 NormalY=0 NormalZ=1 AngleXU=0 Radius=3.0104 StartAngle=2.41495 EndAngle=3.86823
    g29: LineSegment StartX=12.75 StartY=2 StartZ=0 EndX=17.25 EndY=2 EndZ=0
    g30: LineSegment StartX=12.75 StartY=-2 StartZ=0 EndX=17.25 EndY=-2 EndZ=0
    g31: ArcOfCircle CenterX=15 CenterY=0 CenterZ=0 NormalX=0 NormalY=0 NormalZ=1 AngleXU=0 Radius=3.0104 StartAngle=5.55654 EndAngle=7.00983
    g32: ArcOfCircle CenterX=15 CenterY=9.8 CenterZ=0 NormalX=0 NormalY=0 NormalZ=1 AngleXU=0 Radius=3.0104 StartAngle=2.41495 EndAngle=3.86823
    g33: LineSegment StartX=12.75 StartY=11.8 StartZ=0 EndX=17.25 EndY=11.8 EndZ=0
    g34: LineSegment StartX=12.75 StartY=7.8 StartZ=0 EndX=17.25 EndY=7.8 EndZ=0
    g35: ArcOfCircle CenterX=15 CenterY=9.8 CenterZ=0 NormalX=0 NormalY=0 NormalZ=1 AngleXU=0 Radius=3.0104 StartAngle=5.55654 EndAngle=7.00983
    g36: ArcOfCircle CenterX=15 CenterY=19.6 CenterZ=0 NormalX=0 NormalY=0 NormalZ=1 AngleXU=0 Radius=3.0104 StartAngle=2.41495 EndAngle=3.86823
    g37: LineSegment StartX=12.75 StartY=21.6 StartZ=0 EndX=17.25 EndY=21.6 EndZ=0
    g38: LineSegment StartX=12.75 StartY=17.6 StartZ=0 EndX=17.25 EndY=17.6 EndZ=0
    g39: ArcOfCircle CenterX=15 CenterY=19.6 CenterZ=0 NormalX=0 NormalY=0 NormalZ=1 AngleXU=0 Radius=3.0104 StartAngle=5.55654 EndAngle=7.00983
    g40: ArcOfCircle CenterX=15 CenterY=29.4 CenterZ=0 NormalX=0 NormalY=0 NormalZ=1 AngleXU=0 Radius=3.0104 StartAngle=2.41495 EndAngle=3.86823
    g41: LineSegment StartX=12.75 StartY=31.4 StartZ=0 EndX=17.25 EndY=31.4 EndZ=0
    g42: LineSegment StartX=12.75 StartY=27.4 StartZ=0 EndX=17.25 EndY=27.4 EndZ=0
    g43: ArcOfCircle CenterX=15 CenterY=29.4 CenterZ=0 NormalX=0 NormalY=0 NormalZ=1 AngleXU=0 Radius=3.0104 StartAngle=5.55654 EndAngle=7.00983
    g44: ArcOfCircle CenterX=15 CenterY=-9.8 CenterZ=0 NormalX=0 NormalY=0 NormalZ=1 AngleXU=0 Radius=3.0104 StartAngle=2.41495 EndAngle=3.86823
    g45: LineSegment StartX=12.75 StartY=-7.8 StartZ=0 EndX=17.25 EndY=-7.8 EndZ=0
    g46: LineSegment StartX=12.75 StartY=-11.8 StartZ=0 EndX=17.25 EndY=-11.8 EndZ=0
    g47: ArcOfCircle CenterX=15 CenterY=-9.8 CenterZ=0 NormalX=0 NormalY=0 NormalZ=1 AngleXU=0 Radius=3.0104 StartAngle=5.55654 EndAngle=7.00983
    g48: ArcOfCircle CenterX=15 CenterY=-19.6 CenterZ=0 NormalX=0 NormalY=0 NormalZ=1 AngleXU=0 Radius=3.0104 StartAngle=2.41495 EndAngle=3.86823
    g49: LineSegment StartX=12.75 StartY=-17.6 StartZ=0 EndX=17.25 EndY=-17.6 EndZ=0
    g50: LineSegment StartX=12.75 StartY=-21.6 StartZ=0 EndX=17.25 EndY=-21.6 EndZ=0
    g51: ArcOfCircle CenterX=15 CenterY=-19.6 CenterZ=0 NormalX=0 NormalY=0 NormalZ=1 AngleXU=0 Radius=3.0104 StartAngle=5.55654 EndAngle=7.00983
    g52: ArcOfCircle CenterX=15 CenterY=-29.4 CenterZ=0 NormalX=0 NormalY=0 NormalZ=1 AngleXU=0 Radius=3.0104 StartAngle=2.41495 EndAngle=3.86823
    g53: LineSegment StartX=12.75 StartY=-27.4 StartZ=0 EndX=17.25 EndY=-27.4 EndZ=0
    g54: LineSegment StartX=12.75 StartY=-31.4 StartZ=0 EndX=17.25 EndY=-31.4 EndZ=0
    g55: ArcOfCircle CenterX=15 CenterY=-29.4 CenterZ=0 NormalX=0 NormalY=0 NormalZ=1 AngleXU=0 Radius=3.0104 StartAngle=5.55654 EndAngle=7.00983
  constraints (182):
    c: Horizontal(g1)
    c: Horizontal(g2)
    c: PointOnObject(g1,g0)
    c: Coincident(g0,g3)
    c: Coincident(g0,g2)
    c: Coincident(g3,g2)
    c: Coincident(g1,g0)
    c: Coincident(g3,g1)
    c: Equal(g2,g1)
    c: DistanceY(g2,g1) = 4
    c: Horizontal(g5)
    c: Horizontal(g6)
    c: PointOnObject(g5,g4)
    c: Coincident(g4,g7)
    c: Coincident(g4,g6)
    c: Coincident(g7,g6)
    c: Coincident(g5,g4)
    c: Coincident(g7,g5)
    c: Equal(g6,g5)
    c: DistanceY(g6,g5) = 4
    c: Horizontal(g9)
    c: Horizontal(g10)
    c: PointOnObject(g9,g8)
    c: Coincident(g8,g11)
    c: Coincident(g8,g10)
    c: Coincident(g11,g10)
    c: Coincident(g9,g8)
    c: Coincident(g11,g9)
    c: Equal(g10,g9)
    c: DistanceY(g10,g9) = 4
    c: Horizontal(g13)
    c: Horizontal(g14)
    c: PointOnObject(g13,g12)
    c: Coincident(g12,g15)
    c: Coincident(g12,g14)
    c: Coincident(g15,g14)
    c: Coincident(g13,g12)
    c: Coincident(g15,g13)
    c: Equal(g14,g13)
    c: DistanceY(g14,g13) = 4
    c: Horizontal(g17)
    c: Horizontal(g18)
    c: PointOnObject(g17,g16)
    c: Coincident(g16,g19)
    c: Coincident(g16,g18)
    c: Coincident(g19,g18)
    c: Coincident(g17,g16)
    c: Coincident(g19,g17)
    c: Equal(g18,g17)
    c: DistanceY(g18,g17) = 4
    c: Horizontal(g21)
    c: Horizontal(g22)
    c: PointOnObject(g21,g20)
    c: Coincident(g20,g23)
    c: Coincident(g20,g22)
    c: Coincident(g23,g22)
    c: Coincident(g21,g20)
    c: Coincident(g23,g21)
    c: Equal(g22,g21)
    c: DistanceY(g22,g21) = 4
    c: Horizontal(g25)
    c: Horizontal(g26)
    c: PointOnObject(g25,g24)
    c: Coincident(g24,g27)
    c: Coincident(g24,g26)
    c: Coincident(g27,g26)
    c: Coincident(g25,g24)
    c: Coincident(g27,g25)
    c: Equal(g26,g25)
    c: DistanceY(g26,g25) = 4
    c: Vertical(g0,g4)
    c: Vertical(g4,g8)
    c: Vertical(g8,g12)
    c: Vertical(g12,g16)
    c: Vertical(g16,g20)
    c: Vertical(g20,g24)
    c: Equal(g2,g18)
    c: Equal(g18,g22)
    c: Equal(g22,g26)
    c: Equal(g1,g5)
    c: Equal(g5,g9)
    c: Equal(g9,g13)
    c: DistanceY(g8,g12) = 9.8
    c: DistanceY(g4,g8) = 9.8
    c: DistanceY(g0,g4) = 9.8
    c: DistanceY(g16,g0) = 9.8
    c: DistanceY(g20,g16) = 9.8
    c: DistanceY(g24,g20) = 9.8
    c: PointOnObject(g0,g-1)
    c: Horizontal(g29)
    c: Horizontal(g30)
    c: PointOnObject(g29,g28)
    c: Coincident(g28,g31)
    c: Coincident(g28,g30)
    c: Coincident(g31,g30)
    c: Coincident(g29,g28)
    c: Coincident(g31,g29)
    c: Equal(g30,g29)
    c: DistanceY(g30,g29) = 4
    c: Horizontal(g33)
    c: Horizontal(g34)
    c: PointOnObject(g33,g32)
    c: Coincident(g32,g35)
    c: Coincident(g32,g34)
    c: Coincident(g35,g34)
    c: Coincident(g33,g32)
    c: Coincident(g35,g33)
    c: Equal(g34,g33)
    c: DistanceY(g34,g33) = 4
    c: Horizontal(g37)
    c: Horizontal(g38)
    c: PointOnObject(g37,g36)
    c: Coincident(g36,g39)
    c: Coincident(g36,g38)
    c: Coincident(g39,g38)
    c: Coincident(g37,g36)
    c: Coincident(g39,g37)
    c: Equal(g38,g37)
    c: DistanceY(g38,g37) = 4
    c: Horizontal(g41)
    c: Horizontal(g42)
    c: PointOnObject(g41,g40)
    c: Coincident(g40,g43)
    c: Coincident(g40,g42)
    c: Coincident(g43,g42)
    c: Coincident(g41,g40)
    c: Coincident(g43,g41)
    c: Equal(g42,g41)
    c: DistanceY(g42,g41) = 4
    c: Horizontal(g45)
    c: Horizontal(g46)
    c: PointOnObject(g45,g44)
    c: Coincident(g44,g47)
    c: Coincident(g44,g46)
    c: Coincident(g47,g46)
    c: Coincident(g45,g44)
    c: Coincident(g47,g45)
    c: Equal(g46,g45)
    c: DistanceY(g46,g45) = 4
    c: Horizontal(g49)
    c: Horizontal(g50)
    c: PointOnObject(g49,g48)
    c: Coincident(g48,g51)
    c: Coincident(g48,g50)
    c: Coincident(g51,g50)
    c: Coincident(g49,g48)
    c: Coincident(g51,g49)
    c: Equal(g50,g49)
    c: DistanceY(g50,g49) = 4
    c: Horizontal(g53)
    c: Horizontal(g54)
    c: PointOnObject(g53,g52)
    c: Coincident(g52,g55)
    c: Coincident(g52,g54)
    c: Coincident(g55,g54)
    c: Coincident(g53,g52)
    c: Coincident(g55,g53)
    c: Equal(g54,g53)
    c: DistanceY(g54,g53) = 4
    c: Vertical(g28,g32)
    c: Vertical(g32,g36)
    c: Vertical(g36,g40)
    c: Vertical(g40,g44)
    c: Vertical(g44,g48)
    c: Vertical(g48,g52)
    c: Equal(g30,g46)
    c: Equal(g46,g50)
    c: Equal(g50,g54)
    c: Equal(g29,g33)
    c: Equal(g33,g37)
    c: Equal(g37,g41)
    c: DistanceY(g36,g40) = 9.8
    c: DistanceY(g32,g36) = 9.8
    c: DistanceY(g28,g32) = 9.8
    c: DistanceY(g44,g28) = 9.8
    c: DistanceY(g48,g44) = 9.8
    c: DistanceY(g52,g48) = 9.8
    c: PointOnObject(g28,g-1)
    c: DistanceX(g24,g26) = 4.5
    c: DistanceX(g52,g54) = 4.5
    c: DistanceX(g-1,g28) = 15
    c: DistanceX(g28,g0) = 14
FEATURE [PartDesign::Pocket] Pocket  label="PiercesPocket"
  BaseFeature = -> Pad
  Direction = (-2e-16,2e-16,1)
  Length = 69.4
  Length2 = 5
  Midplane = true
  Profile = -> Sketch
  ReferenceAxis = -> Sketch [N_Axis]
  Type = 0
  expr: Length = Spreadsheet.mmBaseWidth + Spreadsheet.mmCellWall * 2
FEATURE [PartDesign::Body] Body004  label="BeamFixator"
  Group = -> [Sketch022,Pad,Sketch,Pocket]
  Origin = -> Origin005
  Tip = -> Pocket
COMPONENT P1 — recipe-attached ("HingePart", modeled in this document).
Construction recipe (the document's own serialized feature program — sketch geometry with constraints, then the solid features built on it; lengths are millimeters unless a unit is written):

FEATURE [PartDesign::LinearPattern] LinearPattern
  Direction = -> Sketch007 [V_Axis]
  Length = 67.8
  Occurrences = 4
  Originals = -> [Revolution,Revolution004,Pocket001,Pocket002,Pad008,Pad009,Pad010,Pad011,Pocket004,Pocket005]
  expr: Length = Spreadsheet.mmHingeHight
  expr: Occurrences = Spreadsheet.nHingeHightDiskCnt
FEATURE [PartDesign::Body] Body005
  Group = -> [LinearPattern]
  Origin = -> Origin007
  Tip = -> LinearPattern
COMPONENT P2 — recipe-attached ("AxisFixatorPart", modeled in this document).
Construction recipe (the document's own serialized feature program — sketch geometry with constraints, then the solid features built on it; lengths are millimeters unless a unit is written):

FEATURE [Sketcher::SketchObject] Sketch027  label="CommonFixatorScatch"
  FullyConstrained = false
  MapMode = 5
  Placement = pos=(0,0,0) rot=(0.57735,0.57735,0.57735;2.0944rad)
  Support = -> [YZ_Plane013]
  expr: Constraints[0] = Spreadsheet.mmAxisTubeDia + 2 * Spreadsheet.mmFixatorThick + 2 * Spreadsheet.mmTwoSideTapeThick
  expr: Constraints[17] = Spreadsheet.mmAxisTubeDia / 2 + Spreadsheet.mmPetalHightMax + Spreadsheet.mmTwoSideTapeThick
  expr: Constraints[18] = Spreadsheet.mmAxisTubeDia / 2 + Spreadsheet.mmPetalHightMax + Spreadsheet.mmTwoSideTapeThick
  expr: Constraints[32] = Spreadsheet.mmPetalPocketWidth
  expr: Constraints[33] = Spreadsheet.mmBaseWidth
  expr: Constraints[3] = Spreadsheet.mmAxisTubeDia
  sketch-geometry (14):
    g0: Circle CenterX=0 CenterY=0 CenterZ=0 NormalX=0 NormalY=0 NormalZ=1 AngleXU=0 Radius=26.72
    g1: LineSegment StartX=0 StartY=0 StartZ=0 EndX=32.2586 EndY=18.6245 EndZ=0
    g2: ArcOfCircle CenterX=0 CenterY=0 CenterZ=0 NormalX=0 NormalY=0 NormalZ=1 AngleXU=0 Radius=20.4 StartAngle=5.32461 EndAngle=6.86682
    g3: LineSegment StartX=-3.7e-15 StartY=-20.4 StartZ=0 EndX=-3.7e-15 EndY=-39.1443 EndZ=0
    g4: LineSegment StartX=-3.7e-15 StartY=-39.1443 StartZ=0 EndX=6.1902 EndY=-42.7183 EndZ=0
    g5: LineSegment StartX=6.1902 StartY=-42.7183 StartZ=0 EndX=40.0902 EndY=15.9983 EndZ=0
    g6: LineSegment StartX=40.0902 StartY=15.9983 StartZ=0 EndX=33.9 EndY=19.5722 EndZ=0
    g7: LineSegment StartX=33.9 StartY=19.5722 StartZ=0 EndX=17.6669 EndY=10.2 EndZ=0
    g8: LineSegment StartX=14.7156 StartY=-14.1284 StartZ=0 EndX=17.9224 EndY=-19.6828 EndZ=0
    g9: LineSegment StartX=17.9224 StartY=-19.6828 StartZ=0 EndX=8.08455 EndY=-25.3627 EndZ=0
    g10: LineSegment StartX=8.08455 StartY=-25.3627 StartZ=0 EndX=4.87772 EndY=-19.8083 EndZ=0
    g11: ArcOfCircle CenterX=0 CenterY=0 CenterZ=0 NormalX=0 NormalY=0 NormalZ=1 AngleXU=0 Radius=20.4 StartAngle=4.71239 EndAngle=4.95383
    g12: ArcOfCircle CenterX=0 CenterY=0 CenterZ=0 NormalX=0 NormalY=0 NormalZ=1 AngleXU=0 Radius=20.4 StartAngle=5.51814 EndAngle=6.80678
    g13: LineSegment StartX=0 StartY=0 StartZ=0 EndX=18.7992 EndY=-32.5612 EndZ=0
  constraints (39):
    c: Diameter(g0) = 53.44
    c: Angle(g-1,g1) = 0.523599
    c: PointOnObject(g6,g1)
    c: Diameter(g2) = 40.8
    c: Vertical(g3)
    c: Coincident(g3,g4)
    c: Coincident(g4,g5)
    c: Coincident(g5,g6)
    c: Coincident(g6,g7)
    c: Coincident(g8,g9)
    c: Coincident(g9,g10)
    c: Equal(g2,g11)
    c: Coincident(g2,g11)
    c: PointOnObject(g3,g-2)
    c: Parallel(g4,g6)
    c: Perpendicular(g5,g4)
    c: Tangent(g0,g5)
    c: Distance(g8,g11) = 26.62
    c: Distance(g9,g11) = 26.62
    c: Coincident(g11,g12)
    c: PointOnObject(g7,g1)
    c: Coincident(g10,g11)
    c: Coincident(g11,g3)
    c: Coincident(g12,g8)
    c: PointOnObject(g12,g1)
    c: Coincident(g12,g7)
    c: PointOnObject(g7,g1)
    c: Perpendicular(g10,g9)
    c: Perpendicular(g9,g8)
    c: Coincident(g13,g11)
    c: Angle(g13,g-1) = 1.0472
    c: Symmetric(g10,g8,g13)
    c: Distance(g10,g8) = 11.3598
    c: Distance(g4,g5) = 67.8
    c: Equal(g4,g6)
    c: Equal(g3,g7)
    c: Coincident(g-1,g0)
    c: Coincident(g0,g11)
    c: Coincident(g11,g1)
FEATURE [PartDesign::Pad] Pad012  label="AxisFixatorBodyPad"
  Direction = (1,-2e-16,3e-16)
  Length = 20.4
  Length2 = 10
  Placement = pos=(0,0,0) rot=(0.57735,0.57735,0.57735;2.0944rad)
  Profile = -> Sketch027
  ReferenceAxis = -> Sketch027 [N_Axis]
  Type = 0
  expr: Length = Spreadsheet.mmFixatorHight
FEATURE [Sketcher::SketchObject] Sketch031  label="MaxPetalBase001"
  FullyConstrained = true
  MapMode = 5
  Placement = pos=(0,0,0) rot=(0.57735,0.57735,0.57735;2.0944rad)
  Support = -> [YZ_Plane013]
  expr: Constraints[3] = Spreadsheet.mmAxisTubeDia / 2 + Spreadsheet.mmPetalHightMax
  expr: Constraints[6] = Spreadsheet.mmAxisTubeDia
  expr: Constraints[8] = Spreadsheet.mmPetalPocketWidth
  sketch-geometry (4):
    g0: LineSegment StartX=19.5933 StartY=5.67991 StartZ=0 EndX=26.52 EndY=5.67991 EndZ=0
    g1: LineSegment StartX=26.52 StartY=5.67991 StartZ=0 EndX=26.52 EndY=-5.67991 EndZ=0
    g2: LineSegment StartX=26.52 StartY=-5.67991 StartZ=0 EndX=19.5933 EndY=-5.67991 EndZ=0
    g3: ArcOfCircle CenterX=0 CenterY=2.5e-15 CenterZ=0 NormalX=0 NormalY=0 NormalZ=1 AngleXU=0 Radius=20.4 StartAngle=6.00103 EndAngle=6.56534
  constraints (12):
    c: Coincident(g0,g1)
    c: Coincident(g1,g2)
    c: Vertical(g1)
    c: DistanceX(g-1,g1) = 26.52
    c: Coincident(g3,g0)
    c: Coincident(g3,g2)
    c: Diameter(g3) = 40.8
    c: Symmetric(g0,g2,g-1)
    c: DistanceY(g2,g0) = 11.3598
    c: Horizontal(g0)
    c: Horizontal(g2)
    c: Coincident(g-1,g3)
FEATURE [Sketcher::SketchObject] Sketch032  label="MinPetalBase001"
  AttachmentOffset = pos=(0,0,18.36) rot=(0,0,1;0rad)
  FullyConstrained = true
  MapMode = 5
  Placement = pos=(18.36,-4.1e-15,4.1e-15) rot=(0.57735,0.57735,0.57735;2.0944rad)
  Support = -> [YZ_Plane013]
  expr: .AttachmentOffset.Base.z = Spreadsheet.mmFixatorHight * 0.9
  expr: Constraints[3] = Spreadsheet.mmAxisTubeDia / 2 + Spreadsheet.mmPetalHightMin
  expr: Constraints[6] = Spreadsheet.mmAxisTubeDia
  expr: Constraints[8] = Spreadsheet.mmPetalPocketWidth
  sketch-geometry (4):
    g0: LineSegment StartX=19.5933 StartY=5.67991 StartZ=0 EndX=23.46 EndY=5.67991 EndZ=0
    g1: LineSegment StartX=23.46 StartY=5.67991 StartZ=0 EndX=23.46 EndY=-5.67991 EndZ=0
    g2: LineSegment StartX=23.46 StartY=-5.67991 StartZ=0 EndX=19.5933 EndY=-5.67991 EndZ=0
    g3: ArcOfCircle CenterX=0 CenterY=2e-15 CenterZ=0 NormalX=0 NormalY=0 NormalZ=1 AngleXU=0 Radius=20.4 StartAngle=6.00103 EndAngle=6.56534
  constraints (12):
    c: Coincident(g0,g1)
    c: Coincident(g1,g2)
    c: Vertical(g1)
    c: DistanceX(g-1,g1) = 23.46
    c: Coincident(g3,g0)
    c: Coincident(g3,g2)
    c: Diameter(g3) = 40.8
    c: Symmetric(g0,g2,g-1)
    c: DistanceY(g2,g0) = 11.3598
    c: Horizontal(g2)
    c: Horizontal(g0)
    c: Coincident(g-1,g3)
FEATURE [PartDesign::SubtractiveLoft] SubtractiveLoft  label="PetalBodySubtractiveLoft"
  BaseFeature = -> Pad012
  Closed = false
  Placement = pos=(0,0,0) rot=(0.57735,0.57735,0.57735;2.0944rad)
  Profile = -> Sketch031
  Ruled = false
  Sections = -> [Sketch032]
FEATURE [PartDesign::PolarPattern] PolarPattern  label="ExisFixatorBodyPolarPattern"
  Angle = 360
  Axis = -> Sketch027 [N_Axis]
  BaseFeature = -> SubtractiveLoft
  Occurrences = 3
  Originals = -> [Pad012,AdditiveLoft,SubtractiveLoft]
  Placement = pos=(0,0,0) rot=(0.57735,0.57735,0.57735;2.0944rad)
FEATURE [PartDesign::Chamfer] Chamfer001
  Angle = 45
  Base = -> PolarPattern [Edge38,Edge9,Edge5,Edge23,Edge65,Edge59,Edge69,Edge47,Edge41]
  BaseFeature = -> PolarPattern
  ChamferType = 1
  FlipDirection = false
  Placement = pos=(0,0,0) rot=(0.57735,0.57735,0.57735;2.0944rad)
  Size = 2
  Size2 = 1
  SupportTransform = false
  UseAllEdges = false
FEATURE [PartDesign::Body] Body007  label="AxisFixatorBody"
  Group = -> [Sketch027,Pad012,Sketch031,Sketch032,SubtractiveLoft,PolarPattern,Chamfer001]
  Origin = -> Origin013
  Tip = -> Chamfer001
COMPONENT P3 — recipe-attached ("PetalMountingTemplate", modeled in this document).
Construction recipe (the document's own serialized feature program — sketch geometry with constraints, then the solid features built on it; lengths are millimeters unless a unit is written):

FEATURE [Sketcher::SketchObject] Sketch035  label="CommonFixatorScatch001"
  AttachmentOffset = pos=(0,0,16.32) rot=(0,0,1;0rad)
  FullyConstrained = false
  MapMode = 5
  Placement = pos=(16.32,-3.6e-15,3.6e-15) rot=(0.57735,0.57735,0.57735;2.0944rad)
  Support = -> [YZ_Plane013]
  expr: .AttachmentOffset.Base.z = Spreadsheet.mmFixatorHight * 0.8
  expr: Constraints[0] = Spreadsheet.mmAxisTubeDia + 2 * Spreadsheet.mmFixatorThick
  expr: Constraints[24] = Spreadsheet.mmBaseWidth
  expr: Constraints[3] = Spreadsheet.mmAxisTubeDia
  sketch-geometry (9):
    g0: Circle CenterX=0 CenterY=0 CenterZ=0 NormalX=0 NormalY=0 NormalZ=1 AngleXU=0 Radius=26.62
    g1: LineSegment StartX=0 StartY=0 StartZ=0 EndX=49.303 EndY=28.4651 EndZ=0
    g2: ArcOfCircle CenterX=0 CenterY=0 CenterZ=0 NormalX=0 NormalY=0 NormalZ=1 AngleXU=0 Radius=20.4 StartAngle=4.71235 EndAngle=6.7955
    g3: LineSegment StartX=-3.7e-15 StartY=-20.4 StartZ=0 EndX=-3.7e-15 EndY=-39.1443 EndZ=0
    g4: LineSegment StartX=-3.7e-15 StartY=-39.1443 StartZ=0 EndX=6.1036 EndY=-42.6683 EndZ=0
    g5: LineSegment StartX=6.1036 StartY=-42.6683 StartZ=0 EndX=40.0036 EndY=16.0483 EndZ=0
    g6: LineSegment StartX=40.0036 StartY=16.0483 StartZ=0 EndX=33.9 EndY=19.5722 EndZ=0
    g7: LineSegment StartX=33.9 StartY=19.5722 StartZ=0 EndX=17.6669 EndY=10.2 EndZ=0
    g8: ArcOfCircle CenterX=0 CenterY=0 CenterZ=0 NormalX=0 NormalY=0 NormalZ=1 AngleXU=0 Radius=20.4 StartAngle=4.71239 EndAngle=6.80678
  constraints (25):
    c: Diameter(g0) = 53.24
    c: Angle(g-1,g1) = 0.523599
    c: PointOnObject(g6,g1)
    c: Diameter(g2) = 40.8
    c: Vertical(g3)
    c: Coincident(g3,g4)
    c: Coincident(g4,g5)
    c: Coincident(g5,g6)
    c: Coincident(g6,g7)
    c: PointOnObject(g3,g-2)
    c: Parallel(g4,g6)
    c: Perpendicular(g5,g4)
    c: Tangent(g0,g5)
    c: PointOnObject(g8,g1)
    c: Coincident(g8,g7)
    c: PointOnObject(g8,g-2)
    c: PointOnObject(g8,g-1)
    c: PointOnObject(g8,g2)
    c: Coincident(g3,g8)
    c: Equal(g4,g6)
    c: Equal(g7,g3)
    c: Coincident(g2,g1)
    c: Coincident(g8,g1)
    c: Coincident(g8,g0)
    c: Distance(g4,g5) = 67.8
FEATURE [PartDesign::Pad] Pad013  label="AxisFixatorBodyPad001"
  Direction = (1,-2e-16,3e-16)
  Length = 6.12
  Length2 = 10
  Placement = pos=(0,0,0) rot=(0.57735,0.57735,0.57735;2.0944rad)
  Profile = -> Sketch035
  ReferenceAxis = -> Sketch035 [N_Axis]
  Type = 0
  expr: Length = Spreadsheet.mmFixatorHight * 0.3
FEATURE [Sketcher::SketchObject] Sketch038  label="MaxPetalBase004"
  FullyConstrained = true
  MapMode = 5
  Placement = pos=(0,0,0) rot=(0.57735,0.57735,0.57735;2.0944rad)
  Support = -> [YZ_Plane013]
  expr: Constraints[11] = Spreadsheet.mmPetalPocketWidth
  expr: Constraints[3] = Spreadsheet.mmAxisTubeDia * 2
  expr: Constraints[6] = Spreadsheet.mmAxisTubeDia
  sketch-geometry (4):
    g0: LineSegment StartX=19.5933 StartY=5.67991 StartZ=0 EndX=81.6 EndY=5.67991 EndZ=0
    g1: LineSegment StartX=81.6 StartY=5.67991 StartZ=0 EndX=81.6 EndY=-5.67991 EndZ=0
    g2: LineSegment StartX=81.6 StartY=-5.67991 StartZ=0 EndX=19.5933 EndY=-5.67991 EndZ=0
    g3: ArcOfCircle CenterX=0 CenterY=2.5e-15 CenterZ=0 NormalX=0 NormalY=0 NormalZ=1 AngleXU=0 Radius=20.4 StartAngle=6.00103 EndAngle=6.56534
  constraints (12):
    c: Coincident(g0,g1)
    c: Coincident(g1,g2)
    c: Vertical(g1)
    c: DistanceX(g-1,g1) = 81.6
    c: Coincident(g3,g0)
    c: Coincident(g3,g2)
    c: Diameter(g3) = 40.8
    c: Horizontal(g0)
    c: Horizontal(g2)
    c: PointOnObject(g3,g-2)
    c: Symmetric(g0,g2,g-1)
    c: DistanceY(g2,g0) = 11.3598
FEATURE [Sketcher::SketchObject] Sketch039  label="MinPetalBase003"
  AttachmentOffset = pos=(0,0,20.4) rot=(0,0,1;0rad)
  FullyConstrained = true
  MapMode = 5
  Placement = pos=(20.4,-4.5e-15,4.5e-15) rot=(0.57735,0.57735,0.57735;2.0944rad)
  Support = -> [YZ_Plane013]
  expr: .AttachmentOffset.Base.z = Spreadsheet.mmFixatorHight
  expr: Constraints[3] = Spreadsheet.mmAxisTubeDia * 2
  expr: Constraints[6] = Spreadsheet.mmAxisTubeDia
  expr: Constraints[7] = Spreadsheet.mmPetalPocketWidth
  sketch-geometry (4):
    g0: LineSegment StartX=19.5933 StartY=5.67991 StartZ=0 EndX=81.6 EndY=5.67991 EndZ=0
    g1: LineSegment StartX=81.6 StartY=5.67991 StartZ=0 EndX=81.6 EndY=-5.67991 EndZ=0
    g2: LineSegment StartX=81.6 StartY=-5.67991 StartZ=0 EndX=19.5933 EndY=-5.67991 EndZ=0
    g3: ArcOfCircle CenterX=0 CenterY=2.1e-15 CenterZ=0 NormalX=0 NormalY=0 NormalZ=1 AngleXU=0 Radius=20.4 StartAngle=6.00103 EndAngle=6.56534
  constraints (12):
    c: Coincident(g0,g1)
    c: Coincident(g1,g2)
    c: Vertical(g1)
    c: DistanceX(g-1,g1) = 81.6
    c: Coincident(g3,g0)
    c: Coincident(g3,g2)
    c: Diameter(g3) = 40.8
    c: DistanceY(g2,g0) = 11.3598
    c: Symmetric(g0,g2,g-1)
    c: Coincident(g-1,g3)
    c: Horizontal(g0)
    c: Horizontal(g2)
FEATURE [PartDesign::SubtractiveLoft] SubtractiveLoft001  label="PetalBodySubtractiveLoft001"
  BaseFeature = -> Pad013
  Closed = false
  Placement = pos=(0,0,0) rot=(0.57735,0.57735,0.57735;2.0944rad)
  Profile = -> Sketch038
  Ruled = false
  Sections = -> [Sketch039]
FEATURE [PartDesign::PolarPattern] PolarPattern001  label="ExisFixatorBodyPolarPattern001"
  Angle = 360
  Axis = -> Sketch035 [N_Axis]
  BaseFeature = -> SubtractiveLoft001
  Occurrences = 3
  Originals = -> [Pad013,SubtractiveLoft001]
  Placement = pos=(0,0,0) rot=(0.57735,0.57735,0.57735;2.0944rad)
FEATURE [Sketcher::SketchObject] Sketch040  label="CommonFixatorScatch002"
  AttachmentOffset = pos=(0,0,16.32) rot=(0,0,1;0rad)
  FullyConstrained = true
  MapMode = 5
  Placement = pos=(16.32,-3.6e-15,3.6e-15) rot=(0.57735,0.57735,0.57735;2.0944rad)
  Support = -> [YZ_Plane013]
  expr: .AttachmentOffset.Base.z = Spreadsheet.mmFixatorHight * 0.8
  expr: Constraints[11] = Spreadsheet.mmAxisTubeDia * 2
  expr: Constraints[14] = Spreadsheet.mmTemplatePartsConnectorDia - 2 * Spreadsheet.mmAirSpace
  expr: Constraints[15] = Spreadsheet.mmTemplatePartsConnectorDia * 3 / 2
  expr: Constraints[1] = Spreadsheet.mmAxisTubeDia + 2 * Spreadsheet.mmFixatorThick
  expr: Constraints[27] = Spreadsheet.mmAirSpace
  expr: Constraints[33] = Spreadsheet.mmTemplatePartsConnectorDia / 3
  expr: Constraints[41] = Spreadsheet.mmTemplatePartsConnectorDia
  expr: Constraints[43] = Spreadsheet.mmTemplatePartsConnectorDia * 2 / 3
  expr: Constraints[45] = Spreadsheet.mmTemplatePartsConnectorDia * 2 / 3 - 2 * Spreadsheet.mmAirSpace
  expr: Constraints[52] = Spreadsheet.mmTemplatePartsConnectorDia / 3
  expr: Constraints[55] = Spreadsheet.mmTemplatePartsConnectorDia / 2
  sketch-geometry (19):
    g0: Circle CenterX=0 CenterY=0 CenterZ=0 NormalX=0 NormalY=0 NormalZ=1 AngleXU=0 Radius=40.8
    g1: Circle CenterX=0 CenterY=0 CenterZ=0 NormalX=0 NormalY=0 NormalZ=1 AngleXU=0 Radius=26.62
    g2: LineSegment StartX=-35.5321 StartY=20.0526 StartZ=0 EndX=-28.3499 EndY=15.9059 EndZ=0
    g3: LineSegment StartX=22.767 StartY=-13.6064 StartZ=0 EndX=23.167 EndY=-12.9136 EndZ=0
    g4: LineSegment StartX=23.167 StartY=-12.9136 StartZ=0 EndX=21.4554 EndY=-11.9254 EndZ=0
    g5: LineSegment StartX=-35.1321 StartY=20.7454 StartZ=0 EndX=-35.5321 EndY=20.0526 EndZ=0
    g6: LineSegment StartX=23.0536 StartY=-13.31 StartZ=0 EndX=-35.3338 EndY=20.4 EndZ=0
    g7: ArcOfCircle CenterX=-26.42 CenterY=17.1754 CenterZ=0 NormalX=0 NormalY=0 NormalZ=1 AngleXU=0 Radius=2.31 StartAngle=4.65418 EndAngle=10.0066
    g8: LineSegment StartX=-26.5543 StartY=14.8693 StartZ=0 EndX=18.3629 EndY=-11.0637 EndZ=0
    g9: LineSegment StartX=-29.5129 StartY=17.5011 StartZ=0 EndX=-35.1321 EndY=20.7454 EndZ=0
    g10: LineSegment StartX=-35.1321 StartY=20.7454 StartZ=0 EndX=-35.5321 EndY=20.0526 EndZ=0
    g11: LineSegment StartX=-35.5321 StartY=20.0526 StartZ=0 EndX=22.851 EndY=-13.6549 EndZ=0
    g12: LineSegment StartX=22.851 StartY=-13.6549 StartZ=0 EndX=23.251 EndY=-12.9621 EndZ=0
    g13: LineSegment StartX=23.251 StartY=-12.9621 StartZ=0 EndX=-35.1321 EndY=20.7454 EndZ=0
    g14: ArcOfCircle CenterX=-26.42 CenterY=17.1754 CenterZ=0 NormalX=0 NormalY=0 NormalZ=1 AngleXU=0 Radius=3.11 StartAngle=5.34093 EndAngle=9.31984
    g15: ArcOfCircle CenterX=20.188 CenterY=-12.0474 CenterZ=0 NormalX=0 NormalY=0 NormalZ=1 AngleXU=0 Radius=2.07333 StartAngle=2.64723 EndAngle=5.73035
    g16: ArcOfCircle CenterX=20.188 CenterY=-12.0474 CenterZ=0 NormalX=0 NormalY=0 NormalZ=1 AngleXU=0 Radius=1.27333 StartAngle=1.99844 EndAngle=6.37914
    g17: LineSegment StartX=21.9524 StartY=-13.1361 StartZ=0 EndX=22.767 EndY=-13.6064 EndZ=0
    g18: LineSegment StartX=19.6599 StartY=-10.8888 StartZ=0 EndX=-24.5914 EndY=14.6597 EndZ=0
  constraints (56):
    c: PointOnObject(g6,g0)
    c: Diameter(g1) = 53.24
    c: Coincident(g0,g1)
    c: Coincident(g0,g-1)
    c: Coincident(g3,g4)
    c: Coincident(g9,g5)
    c: Coincident(g5,g2)
    c: Perpendicular(g3,g2)
    c: Symmetric(g2,g9,g6)
    c: Symmetric(g17,g3,g6)
    c: PointOnObject(g0,g6)
    c: Diameter(g0) = 81.6
    c: PointOnObject(g6,g1)
    c: Angle(g-1,g6) = 2.61799
    c: Diameter(g7) = 4.62
    c: Distance(g7,g5) = 9.33
    c: Parallel(g9,g4)
    c: Parallel(g2,g8)
    c: Coincident(g10,g11)
    c: Coincident(g11,g12)
    c: Coincident(g12,g13)
    c: Coincident(g13,g10)
    c: PointOnObject(g10,g0)
    c: Symmetric(g10,g10,g6)
    c: Parallel(g6,g13)
    c: Parallel(g11,g13)
    c: Coincident(g5,g10)
    c: Distance(g3,g3) = 0.8
    c: Coincident(g3,g17)
    c: PointOnObject(g11,g1)
    c: PointOnObject(g12,g1)
    c: PointOnObject(g3,g13)
    c: Distance(g6,g3) = 0.1
    c: Distance(g2,g8) = 2.07333
    c: PointOnObject(g14,g13)
    c: PointOnObject(g14,g13)
    c: PointOnObject(g18,g14)
    c: PointOnObject(g9,g14)
    c: Coincident(g7,g8)
    c: Coincident(g7,g2)
    c: Coincident(g14,g7)
    c: Diameter(g14) = 6.22
    c: PointOnObject(g18,g13)
    c: Diameter(g15) = 4.14667
    c: Coincident(g15,g16)
    c: Diameter(g16) = 2.54667
    c: Coincident(g15,g8)
    c: PointOnObject(g8,g11)
    c: Coincident(g17,g15)
    c: PointOnObject(g15,g11)
    c: Coincident(g4,g16)
    c: Coincident(g18,g16)
    c: Distance(g16,g4) = 2.07333
    c: PointOnObject(g4,g13)
    c: PointOnObject(g16,g13)
    c: Distance(g15,g12) = 3.11
FEATURE [PartDesign::Pocket] Pocket003
  BaseFeature = -> PolarPattern001
  Direction = (-1,2e-16,-3e-16)
  Length = 40.8
  Length2 = 5
  Midplane = true
  Placement = pos=(0,0,0) rot=(0.57735,0.57735,0.57735;2.0944rad)
  Profile = -> Sketch040
  ReferenceAxis = -> Sketch040 [N_Axis]
  Type = 0
  expr: Length = Spreadsheet.mmAxisTubeDia
FEATURE [PartDesign::Chamfer] Chamfer002
  Angle = 45
  Base = -> Pocket003 [Edge1,Edge35,Edge31,Edge98,Edge94,Edge47,Edge12]
  BaseFeature = -> Pocket003
  ChamferType = 0
  FlipDirection = false
  Placement = pos=(0,0,0) rot=(0.57735,0.57735,0.57735;2.0944rad)
  Size = 1
  Size2 = 1
  SupportTransform = false
  UseAllEdges = false
FEATURE [PartDesign::Chamfer] Chamfer003
  Angle = 45
  Base = -> Chamfer002 [Edge56,Edge17,Edge3,Edge28]
  BaseFeature = -> Chamfer002
  ChamferType = 0
  FlipDirection = false
  Placement = pos=(0,0,0) rot=(0.57735,0.57735,0.57735;2.0944rad)
  Size = 1
  Size2 = 1
  SupportTransform = false
  UseAllEdges = false
FEATURE [PartDesign::Chamfer] Chamfer004
  Angle = 45
  Base = -> Chamfer003 [Edge56,Edge61,Edge130,Edge128,Edge73,Edge75]
  BaseFeature = -> Chamfer003
  ChamferType = 0
  FlipDirection = false
  Placement = pos=(0,0,0) rot=(0.57735,0.57735,0.57735;2.0944rad)
  Size = 1
  Size2 = 1
  SupportTransform = false
  UseAllEdges = false
FEATURE [PartDesign::Fillet] Fillet
  Base = -> Chamfer004 [Edge66,Edge26]
  BaseFeature = -> Chamfer004
  Placement = pos=(0,0,0) rot=(0.57735,0.57735,0.57735;2.0944rad)
  Radius = 1
  SupportTransform = false
  UseAllEdges = false
FEATURE [PartDesign::Body] Body010  label="AxisFixatorTemplate"
  Group = -> [Sketch035,Pad013,Sketch038,Sketch039,SubtractiveLoft001,PolarPattern001,Sketch040,Pocket003,Chamfer002,Chamfer003,Chamfer004,Fillet]
  Origin = -> Origin019
  Tip = -> Fillet
COMPONENT P4 — recipe-attached ("AxisFixatorAbsolete", modeled in this document).
Construction recipe (the document's own serialized feature program — sketch geometry with constraints, then the solid features built on it; lengths are millimeters unless a unit is written):

FEATURE [Sketcher::SketchObject] Sketch041  label="CommonFixatorScatch003"
  FullyConstrained = false
  MapMode = 5
  Placement = pos=(0,0,0) rot=(0.57735,0.57735,0.57735;2.0944rad)
  Support = -> [YZ_Plane013]
  expr: Constraints[22] = 2 * (Spreadsheet.mmAxisTubeDia / 2 + Spreadsheet.mmFixatorThick) / cos(Spreadsheet.angPetal / 2)
  expr: Constraints[23] = Spreadsheet.mmHingeHight
  expr: Constraints[31] = Spreadsheet.mmAxisTubeDia
  expr: Constraints[64] = Spreadsheet.mmPetalWidth + Spreadsheet.mmAirSpace
  expr: Constraints[67] = Spreadsheet.mmAxisTubeDia / 2 + Spreadsheet.mmPetalHightMax + Spreadsheet.mmTwoSideTapeThick + Spreadsheet.mmAirSpace
  sketch-geometry (24):
    g0: LineSegment StartX=33.9 StartY=19.5722 StartZ=0 EndX=-33.9 EndY=19.5722 EndZ=0
    g1: LineSegment StartX=-33.9 StartY=19.5722 StartZ=0 EndX=-7.1e-15 EndY=-39.1443 EndZ=0
    g2: LineSegment StartX=-7.1e-15 StartY=-39.1443 StartZ=0 EndX=33.9 EndY=19.5722 EndZ=0
    g3: Circle CenterX=0 CenterY=0 CenterZ=0 NormalX=0 NormalY=0 NormalZ=1 AngleXU=0 Radius=39.1443
    g4: LineSegment StartX=-23.8668 StartY=13.7795 StartZ=0 EndX=-23.8668 EndY=-13.7795 EndZ=0
    g5: LineSegment StartX=-23.8668 StartY=-13.7795 StartZ=0 EndX=0 EndY=-27.5591 EndZ=0
    g6: LineSegment StartX=0 StartY=-27.5591 StartZ=0 EndX=23.8668 EndY=-13.7795 EndZ=0
    g7: LineSegment StartX=23.8668 StartY=-13.7795 StartZ=0 EndX=23.8668 EndY=13.7795 EndZ=0
    g8: LineSegment StartX=23.8668 StartY=13.7795 StartZ=0 EndX=0 EndY=27.5591 EndZ=0
    g9: LineSegment StartX=0 StartY=27.5591 StartZ=0 EndX=-23.8668 EndY=13.7795 EndZ=0
    g10: Circle CenterX=0 CenterY=0 CenterZ=0 NormalX=0 NormalY=0 NormalZ=1 AngleXU=0 Radius=27.5591
    g11: LineSegment StartX=0 StartY=0 StartZ=0 EndX=33.9 EndY=19.5722 EndZ=0
    g12: ArcOfCircle CenterX=0 CenterY=0 CenterZ=0 NormalX=0 NormalY=0 NormalZ=1 AngleXU=0 Radius=20.4 StartAngle=4.5996 EndAngle=6.79538
    g13: LineSegment StartX=-7.1e-15 StartY=-20.4 StartZ=0 EndX=-7.1e-15 EndY=-39.1443 EndZ=0
    g14: LineSegment StartX=-7.1e-15 StartY=-39.1443 StartZ=0 EndX=6.91684 EndY=-43.1378 EndZ=0
    g15: LineSegment StartX=6.91684 StartY=-43.1378 StartZ=0 EndX=40.8168 EndY=15.5787 EndZ=0
    g16: LineSegment StartX=40.8168 StartY=15.5787 StartZ=0 EndX=33.9 EndY=19.5722 EndZ=0
    g17: LineSegment StartX=33.9 StartY=19.5722 StartZ=0 EndX=17.6669 EndY=10.2 EndZ=0
    g18: LineSegment StartX=14.7156 StartY=-14.1284 StartZ=0 EndX=18.6289 EndY=-20.9065 EndZ=0
    g19: LineSegment StartX=18.6289 StartY=-20.9065 StartZ=0 EndX=8.79105 EndY=-26.5864 EndZ=0
    g20: LineSegment StartX=8.79105 StartY=-26.5864 StartZ=0 EndX=4.87772 EndY=-19.8083 EndZ=0
    g21: ArcOfCircle CenterX=0 CenterY=0 CenterZ=0 NormalX=0 NormalY=0 NormalZ=1 AngleXU=0 Radius=20.4 StartAngle=4.71239 EndAngle=4.95383
    g22: ArcOfCircle CenterX=0 CenterY=0 CenterZ=0 NormalX=0 NormalY=0 NormalZ=1 AngleXU=0 Radius=20.4 StartAngle=5.51814 EndAngle=6.80678
    g23: LineSegment StartX=0 StartY=0 StartZ=0 EndX=19.5722 EndY=-33.9 EndZ=0
  constraints (64):
    c: Coincident(g0,g1)
    c: Coincident(g1,g2)
    c: Coincident(g2,g0)
    c: Equal(g0,g1)
    c: Equal(g0,g2)
    c: PointOnObject(g0,g3)
    c: Coincident(g4,g5)
    c: Coincident(g5,g6)
    c: Coincident(g6,g7)
    c: Coincident(g7,g8)
    c: Coincident(g8,g9)
    c: Coincident(g9,g4)
    c: Equal(g4, g5-g9) x5
    c: PointOnObject(g4,g10)
    c: PointOnObject(g5,g10)
    c: PointOnObject(g6,g10)
    c: PointOnObject(g7,g10)
    c: PointOnObject(g8,g10)
    c: Diameter(g10) = 55.1181
    c: Distance(g2) = 67.8
    c: PointOnObject(g5,g-2)
    c: PointOnObject(g4,g10)
    c: Angle(g-1,g11) = 0.523599
    c: Coincident(g3,g10)
    c: Coincident(g3,g11)
    c: Coincident(g3,g-1)
    c: PointOnObject(g0,g11)
    c: Diameter(g12) = 40.8
    c: Coincident(g12,g3)
    c: Vertical(g13)
    c: Coincident(g13,g14)
    c: Coincident(g14,g15)
    c: Coincident(g15,g16)
    c: Coincident(g16,g17)
    c: Coincident(g19,g20)
    c: Coincident(g1,g13)
    c: Coincident(g0,g16)
    c: Equal(g12,g21)
    c: Coincident(g12,g21)
    c: PointOnObject(g13,g-2)
    c: PointOnObject(g13,g3)
    c: Parallel(g2,g15)
    c: Parallel(g14,g16)
    c: Perpendicular(g15,g14)
    c: Tangent(g10,g15)
    c: PointOnObject(g11,g3)
    c: Coincident(g21,g22)
    c: PointOnObject(g17,g11)
    c: Coincident(g20,g21)
    c: Coincident(g21,g13)
    c: Coincident(g22,g18)
    c: PointOnObject(g22,g11)
    c: Coincident(g22,g17)
    c: PointOnObject(g17,g11)
    c: Perpendicular(g20,g19)
    c: Perpendicular(g19,g18)
    c: Coincident(g23,g21)
    c: Angle(g23,g-2) = 2.61799
    c: PointOnObject(g23,g3)
    c: Symmetric(g20,g18,g23)
    c: Distance(g20,g18) = 11.3598
    c: Perpendicular(g23,g19)
    c: Coincident(g18,g19)
    c: Distance(g21,g19) = 27.42
FEATURE [PartDesign::Pad] Pad014  label="AxisFixatorBodyPad002"
  Direction = (1,-2e-16,3e-16)
  Length = 20.4
  Length2 = 10
  Placement = pos=(0,0,0) rot=(0.57735,0.57735,0.57735;2.0944rad)
  Profile = -> Sketch041
  ReferenceAxis = -> Sketch041 [N_Axis]
  Type = 0
  expr: Length = Spreadsheet.mmFixatorHight
FEATURE [Sketcher::SketchObject] Sketch044  label="MaxPetalBase006"
  FullyConstrained = false
  MapMode = 5
  Placement = pos=(0,0,0) rot=(0.57735,0.57735,0.57735;2.0944rad)
  Support = -> [YZ_Plane013]
  expr: Constraints[0] = Spreadsheet.mmAxisTubeDia + 2 * Spreadsheet.mmFixatorThick
  expr: Constraints[14] = Spreadsheet.mmPetalWidth + Spreadsheet.mmAirSpace
  expr: Constraints[1] = Spreadsheet.mmAxisTubeDia
  expr: Constraints[5] = Spreadsheet.mmAxisTubeDia / 2 + Spreadsheet.mmPetalHightMax
  expr: Constraints[9] = Spreadsheet.mmAxisTubeDia
  sketch-geometry (7):
    g0: Circle CenterX=0 CenterY=0 CenterZ=0 NormalX=0 NormalY=0 NormalZ=1 AngleXU=0 Radius=39.855
    g1: Circle CenterX=0 CenterY=0 CenterZ=0 NormalX=0 NormalY=0 NormalZ=1 AngleXU=0 Radius=26.62
    g2: ArcOfCircle CenterX=0 CenterY=0 CenterZ=0 NormalX=0 NormalY=0 NormalZ=1 AngleXU=0 Radius=20.4 StartAngle=5.86249 EndAngle=6.74499
    g3: LineSegment StartX=19.5933 StartY=5.67991 StartZ=0 EndX=26.52 EndY=5.67991 EndZ=0
    g4: LineSegment StartX=26.52 StartY=5.67991 StartZ=0 EndX=26.52 EndY=-5.67991 EndZ=0
    g5: LineSegment StartX=26.52 StartY=-5.67991 StartZ=0 EndX=19.5933 EndY=-5.67991 EndZ=0
    g6: ArcOfCircle CenterX=0 CenterY=0 CenterZ=0 NormalX=0 NormalY=0 NormalZ=1 AngleXU=0 Radius=20.4 StartAngle=6.00103 EndAngle=6.56534
  constraints (22):
    c: Diameter(g1) = 53.24
    c: Diameter(g2) = 40.8
    c: Coincident(g3,g4)
    c: Coincident(g4,g5)
    c: Coincident(g0,g2)
    c: DistanceX(g-1,g4) = 26.52
    c: Coincident(g6,g0)
    c: Coincident(g6,g3)
    c: Coincident(g6,g5)
    c: Diameter(g6) = 40.8
    c: Coincident(g6,g-1)
    c: Symmetric(g3,g5,g-1)
    c: Horizontal(g5)
    c: Horizontal(g3)
    c: DistanceY(g5,g3) = 11.3598
    c: Coincident(g6,g1)
    c: PointOnObject(g6,g-2)
    c: PointOnObject(g6,g-1)
    c: PointOnObject(g6,g5)
    c: PointOnObject(g6,g3)
    c: PointOnObject(g3,g6)
    c: Vertical(g4)
FEATURE [Sketcher::SketchObject] Sketch045  label="MinPetalBase005"
  AttachmentOffset = pos=(0,0,18.36) rot=(0,0,1;0rad)
  FullyConstrained = false
  MapMode = 5
  Placement = pos=(18.36,-4.1e-15,4.1e-15) rot=(0.57735,0.57735,0.57735;2.0944rad)
  Support = -> [YZ_Plane013]
  expr: .AttachmentOffset.Base.z = Spreadsheet.mmFixatorHight * 0.9
  expr: Constraints[0] = Spreadsheet.mmAxisTubeDia + 2 * Spreadsheet.mmFixatorThick
  expr: Constraints[10] = Spreadsheet.mmAxisTubeDia
  expr: Constraints[12] = Spreadsheet.mmPetalWidth + Spreadsheet.mmAirSpace
  expr: Constraints[1] = Spreadsheet.mmAxisTubeDia
  expr: Constraints[6] = Spreadsheet.mmAxisTubeDia / 2 + Spreadsheet.mmPetalHightMin
  sketch-geometry (7):
    g0: Circle CenterX=0 CenterY=2.3e-15 CenterZ=0 NormalX=0 NormalY=0 NormalZ=1 AngleXU=0 Radius=39.844
    g1: Circle CenterX=0 CenterY=2.3e-15 CenterZ=0 NormalX=0 NormalY=0 NormalZ=1 AngleXU=0 Radius=26.62
    g2: ArcOfCircle CenterX=0 CenterY=2.3e-15 CenterZ=0 NormalX=0 NormalY=0 NormalZ=1 AngleXU=0 Radius=20.4 StartAngle=3.8687 EndAngle=6.82101
    g3: LineSegment StartX=19.5933 StartY=5.67991 StartZ=0 EndX=23.46 EndY=5.67991 EndZ=0
    g4: LineSegment StartX=23.46 StartY=5.67991 StartZ=0 EndX=23.46 EndY=-5.67991 EndZ=0
    g5: LineSegment StartX=23.46 StartY=-5.67991 StartZ=0 EndX=19.5933 EndY=-5.67991 EndZ=0
    g6: ArcOfCircle CenterX=0 CenterY=2.3e-15 CenterZ=0 NormalX=0 NormalY=0 NormalZ=1 AngleXU=0 Radius=20.4 StartAngle=6.00103 EndAngle=6.56534
  constraints (17):
    c: Diameter(g1) = 53.24
    c: Diameter(g2) = 40.8
    c: Coincident(g3,g4)
    c: Coincident(g4,g5)
    c: Coincident(g0,g2)
    c: Vertical(g4)
    c: DistanceX(g-1,g4) = 23.46
    c: Coincident(g6,g0)
    c: Coincident(g6,g3)
    c: Coincident(g6,g5)
    c: Diameter(g6) = 40.8
    c: Symmetric(g3,g5,g-1)
    c: DistanceY(g5,g3) = 11.3598
    c: Horizontal(g3)
    c: Horizontal(g5)
    c: Coincident(g6,g1)
    c: Coincident(g6,g-1)
FEATURE [PartDesign::SubtractiveLoft] SubtractiveLoft002  label="PetalBodySubtractiveLoft002"
  BaseFeature = -> Pad014
  Closed = false
  Placement = pos=(0,0,0) rot=(0.57735,0.57735,0.57735;2.0944rad)
  Profile = -> Sketch044
  Ruled = false
  Sections = -> [Sketch045]
FEATURE [PartDesign::PolarPattern] PolarPattern002  label="ExisFixatorBodyPolarPattern002"
  Angle = 360
  Axis = -> Sketch041 [N_Axis]
  BaseFeature = -> SubtractiveLoft002
  Occurrences = 3
  Originals = -> [Pad014,SubtractiveLoft002]
  Placement = pos=(0,0,0) rot=(0.57735,0.57735,0.57735;2.0944rad)
FEATURE [PartDesign::Body] Body011  label="AxisFixatorBody001"
  Group = -> [Sketch041,Pad014,Sketch044,Sketch045,SubtractiveLoft002,PolarPattern002]
  Origin = -> Origin021
  Tip = -> PolarPattern002
COMPONENT P5 — recipe-attached ("PulleyOnRotor", modeled in this document).
Construction recipe (the document's own serialized feature program — sketch geometry with constraints, then the solid features built on it; lengths are millimeters unless a unit is written):

FEATURE [Sketcher::SketchObject] Sketch048
  FullyConstrained = true
  MapMode = 5
  Support = -> [XY_Plane019]
  expr: Constraints[1] = Spreadsheet.mmAxisTubeDia
  expr: Constraints[24] = Spreadsheet.mmPulleyExtDia - Spreadsheet.mmPasBaseType
  expr: Constraints[37] = Spreadsheet.mmPasStep
  expr: Constraints[4] = Spreadsheet.mmPulleyExtDia - 2 * Spreadsheet.mmPassToothHight - Spreadsheet.mmPasBaseType * 2
  expr: Constraints[5] = Spreadsheet.mmPulleyExtDia - Spreadsheet.mmPasBaseType * 2
  sketch-geometry (13):
    g0: ArcOfCircle CenterX=0 CenterY=0 CenterZ=0 NormalX=0 NormalY=0 NormalZ=1 AngleXU=0 Radius=20.4 StartAngle=0 EndAngle=0.216246
    g1: Circle CenterX=0 CenterY=0 CenterZ=0 NormalX=0 NormalY=0 NormalZ=1 AngleXU=0 Radius=20.5169
    g2: Circle CenterX=0 CenterY=0 CenterZ=0 NormalX=0 NormalY=0 NormalZ=1 AngleXU=0 Radius=22.4169
    g3: LineSegment StartX=0 StartY=0 StartZ=0 EndX=22.6274 EndY=4.9708 EndZ=0
    g4: LineSegment StartX=0 StartY=0 StartZ=0 EndX=23.1669 EndY=0 EndZ=0
    g5: LineSegment StartX=21.8948 StartY=4.80988 StartZ=0 EndX=19.9249 EndY=4.37712 EndZ=0
    g6: LineSegment StartX=22.4169 StartY=0 StartZ=0 EndX=20.4 EndY=0 EndZ=0
    g7: ArcOfCircle CenterX=20.7228 CenterY=4.5524 CenterZ=0 NormalX=0 NormalY=0 NormalZ=1 AngleXU=0 Radius=1.2 StartAngle=4.82474 EndAngle=6.49943
    g8: ArcOfCircle CenterX=21.2169 CenterY=0 CenterZ=0 NormalX=0 NormalY=0 NormalZ=1 AngleXU=0 Radius=1.2 StartAngle=0 EndAngle=1.67469
    g9: ArcOfCircle CenterX=20.9234 CenterY=2.7741 CenterZ=0 NormalX=0 NormalY=0 NormalZ=1 AngleXU=0 Radius=0.589587 StartAngle=1.68314 EndAngle=3.95806
    g10: ArcOfCircle CenterX=21.0313 CenterY=1.77994 CenterZ=0 NormalX=0 NormalY=0 NormalZ=1 AngleXU=0 Radius=0.589587 StartAngle=2.54137 EndAngle=4.81629
    g11: ArcOfCircle CenterX=20.3971 CenterY=2.21403 CenterZ=0 NormalX=0 NormalY=0 NormalZ=1 AngleXU=0 Radius=0.178959 StartAngle=5.68296 EndAngle=7.09965
    g12: Circle CenterX=0 CenterY=0 CenterZ=0 NormalX=0 NormalY=0 NormalZ=1 AngleXU=0 Radius=23.1669
  constraints (39):
    c: Coincident(g0,g-1)
    c: Diameter(g0) = 40.8
    c: Coincident(g1,g0)
    c: Coincident(g2,g0)
    c: Diameter(g1) = 41.0339
    c: Diameter(g2) = 44.8339
    c: Coincident(g4,g3)
    c: Coincident(g0,g3)
    c: PointOnObject(g6,g0)
    c: PointOnObject(g0,g4)
    c: PointOnObject(g6,g4)
    c: Distance(g7,g5) = 1.2
    c: PointOnObject(g8,g4)
    c: Distance(g8,g6) = 1.2
    c: Equal(g9,g10)
    c: Tangent(g10,g1)
    c: Tangent(g9,g1)
    c: Distance(g9,g10) = 1
    c: Tangent(g9,g7) = 1.5708
    c: Tangent(g8,g10) = 1.5708
    c: PointOnObject(g11,g1)
    c: Tangent(g10,g11) = 1.5708
    c: Tangent(g9,g11) = 1.5708
    c: Coincident(g12,g0)
    c: Diameter(g12) = 46.3339
    c: Coincident(g5,g7)
    c: PointOnObject(g3,g12)
    c: Tangent(g8,g2)
    c: PointOnObject(g8,g4)
    c: PointOnObject(g5,g3)
    c: PointOnObject(g0,g3)
    c: Coincident(g5,g0)
    c: PointOnObject(g7,g3)
    c: Tangent(g7,g2)
    c: PointOnObject(g6,g2)
    c: PointOnObject(g6,g4)
    c: PointOnObject(g4,g12)
    c: Distance(g3,g4) = 5
    c: PointOnObject(g4,g-1)
FEATURE [PartDesign::Pad] Pad015
  Direction = (0,0,1)
  Length = 12
  Length2 = 10
  Midplane = true
  Profile = -> Sketch048
  ReferenceAxis = -> Sketch048 [N_Axis]
  Type = 0
  expr: Length = Spreadsheet.mmPasWidth
FEATURE [PartDesign::PolarPattern] PolarPattern003
  Angle = 360
  Axis = -> Sketch048 [N_Axis]
  BaseFeature = -> Pad015
  Occurrences = 30
  Originals = -> [Pad015]
  expr: Angle = 360
  expr: Occurrences = Spreadsheet.cntPulleyTooth / 2 * 2
FEATURE [PartDesign::Body] Body012  label="PulleyOnRotorBody"
  Group = -> [Sketch048,Pad015,PolarPattern003]
  Origin = -> Origin023
  Tip = -> PolarPattern003
COMPONENT P6 — recipe-attached ("PulleyBorder", modeled in this document).
Construction recipe (the document's own serialized feature program — sketch geometry with constraints, then the solid features built on it; lengths are millimeters unless a unit is written):

FEATURE [Sketcher::SketchObject] Sketch049
  FullyConstrained = false
  MapMode = 5
  Placement = pos=(0,0,0) rot=(1,0,0;1.5708rad)
  Support = -> [XZ_Plane021]
  expr: Constraints[10] = Spreadsheet.mmAxisTubeDia / 2
  expr: Constraints[13] = Spreadsheet.mmPasWidth
  expr: Constraints[16] = Spreadsheet.mmPulleyConnectorThickness
  expr: Constraints[17] = Spreadsheet.mmPulleyConnectorHeight
  expr: Constraints[19] = Spreadsheet.mmPulleyConnectorThickness / 2
  expr: Constraints[9] = (Spreadsheet.mmPulleyExtDia - 2 * Spreadsheet.mmPassToothHight - Spreadsheet.mmPasBaseType * 2) / 2
  sketch-geometry (9):
    g0: LineSegment StartX=20.5169 StartY=6 StartZ=0 EndX=20.4 EndY=6 EndZ=0
    g1: LineSegment StartX=20.4 StartY=6 StartZ=0 EndX=20.4 EndY=-23 EndZ=0
    g2: LineSegment StartX=20.4 StartY=-23 StartZ=0 EndX=24.4 EndY=-23 EndZ=0
    g3: LineSegment StartX=24.4 StartY=-23 StartZ=0 EndX=24.4 EndY=-8 EndZ=0
    g4: LineSegment StartX=24.4 StartY=-8 StartZ=0 EndX=25.7244 EndY=-6.67562 EndZ=0
    g5: LineSegment StartX=25.5272 StartY=-6.17496 StartZ=0 EndX=20.5169 EndY=-6 EndZ=0
    g6: LineSegment StartX=20.5169 StartY=-6 StartZ=0 EndX=20.5169 EndY=6 EndZ=0
    g7: ArcOfCircle CenterX=25.5169 CenterY=-6.46816 CenterZ=0 NormalX=0 NormalY=0 NormalZ=1 AngleXU=0 Radius=0.293382 StartAngle=5.49779 EndAngle=7.81908
    g8: ArcOfCircle CenterX=29.4 CenterY=9.96836 CenterZ=0 NormalX=0 NormalY=0 NormalZ=1 AngleXU=0 Radius=1.7e-15 StartAngle=5.30264 EndAngle=9.80375
  constraints (22):
    c: Horizontal(g0)
    c: Coincident(g0,g1)
    c: Vertical(g1)
    c: Coincident(g1,g2)
    c: Coincident(g2,g3)
    c: Vertical(g3)
    c: Coincident(g3,g4)
    c: Coincident(g5,g6)
    c: Symmetric(g5,g6,g-1)
    c: DistanceX(g-1,g6) = 20.5169
    c: DistanceX(g-1,g1) = 20.4
    c: Horizontal(g2)
    c: Angle(g-1,g4) = 0.785398
    c: DistanceY(g6,g6) = 12
    c: Tangent(g5,g7) = -1.5708
    c: Tangent(g4,g7) = -1.5708
    c: DistanceX(g2,g2) = 4
    c: DistanceY(g3,g3) = 15
    c: Angle(g-1,g5) = 3.10669
    c: DistanceY(g3,g5) = 2
    c: DistanceX(g5,g7) = 5
    c: Coincident(g0,g6)
FEATURE [PartDesign::Revolution] Revolution005
  Angle = 360
  Axis = (0,-2e-16,1)
  Base = (0,0,0)
  Placement = pos=(0,0,0) rot=(1,0,0;1.5708rad)
  Profile = -> Sketch049
  ReferenceAxis = -> Sketch049 [V_Axis]
  expr: Angle = 360
FEATURE [Sketcher::SketchObject] Sketch050
  AttachmentOffset = pos=(0,0,-25) rot=(0,0,1;0rad)
  FullyConstrained = false
  MapMode = 5
  Placement = pos=(0,0,-25) rot=(0,0,1;0rad)
  Support = -> [XY_Plane021]
  expr: .AttachmentOffset.Base.z = -(Spreadsheet.mmPulleyConnectorHeight + Spreadsheet.mmPasWidth / 2 + Spreadsheet.mmPulleyConnectorThickness)
  expr: Constraints[10] = 360 / Spreadsheet.cntPulleyConnectorTooth / 4
  expr: Constraints[11] = Spreadsheet.mmAxisTubeDia + Spreadsheet.mmPulleyConnectorThickness - 2 * Spreadsheet.mmAirSpace
  expr: Constraints[14] = Spreadsheet.mmAirSpace / 2
  expr: Constraints[15] = Spreadsheet.mmAirSpace / 2
  expr: Constraints[23] = Spreadsheet.mmAxisTubeDia + Spreadsheet.mmPulleyConnectorThickness * 2 - Spreadsheet.mmAirSpace / 2
  expr: Constraints[2] = Spreadsheet.mmAxisTubeDia
  expr: Constraints[3] = Spreadsheet.mmAxisTubeDia + Spreadsheet.mmPulleyConnectorThickness * 2
  expr: Constraints[6] = 360 / Spreadsheet.cntPulleyConnectorTooth
  expr: Constraints[9] = 360 / Spreadsheet.cntPulleyConnectorTooth * 3 / 4
  sketch-geometry (14):
    g0: Circle CenterX=0 CenterY=0 CenterZ=0 NormalX=0 NormalY=0 NormalZ=1 AngleXU=0 Radius=20.4
    g1: Circle CenterX=0 CenterY=0 CenterZ=0 NormalX=0 NormalY=0 NormalZ=1 AngleXU=0 Radius=24.4
    g2: LineSegment StartX=0 StartY=0 StartZ=0 EndX=23.5686 EndY=6.31518 EndZ=0
    g3: LineSegment StartX=0 StartY=0 StartZ=0 EndX=23.9312 EndY=4.7602 EndZ=0
    g4: LineSegment StartX=0 StartY=0 StartZ=0 EndX=24.3478 EndY=1.59584 EndZ=0
    g5: ArcOfCircle CenterX=0 CenterY=0 CenterZ=0 NormalX=0 NormalY=0 NormalZ=1 AngleXU=0 Radius=21.6 StartAngle=0.0469303 EndAngle=0.214869
    g6: LineSegment StartX=21.1033 StartY=4.60554 StartZ=0 EndX=23.6537 EndY=5.11285 EndZ=0
    g7: LineSegment StartX=24.171 StartY=1.1834 StartZ=0 EndX=21.5762 EndY=1.01332 EndZ=0
    g8: ArcOfCircle CenterX=0 CenterY=0 CenterZ=0 NormalX=0 NormalY=0 NormalZ=1 AngleXU=0 Radius=24.4 StartAngle=1e-16 EndAngle=0.261799
    g9: ArcOfCircle CenterX=0 CenterY=0 CenterZ=0 NormalX=0 NormalY=0 NormalZ=1 AngleXU=0 Radius=24.2 StartAngle=0 EndAngle=0.0489202
    g10: LineSegment StartX=0 StartY=0 StartZ=0 EndX=30.359 EndY=0 EndZ=0
    g11: LineSegment StartX=24.2 StartY=0 StartZ=0 EndX=24.4 EndY=1.7e-15 EndZ=0
    g12: ArcOfCircle CenterX=0 CenterY=0 CenterZ=0 NormalX=0 NormalY=0 NormalZ=1 AngleXU=0 Radius=24.2 StartAngle=0.212879 EndAngle=0.261799
    g13: LineSegment StartX=23.3754 StartY=6.26342 StartZ=0 EndX=23.5686 EndY=6.31518 EndZ=0
  constraints (38):
    c: Coincident(g0,g-1)
    c: Coincident(g1,g0)
    c: Diameter(g0) = 40.8
    c: Diameter(g1) = 48.8
    c: Coincident(g2,g0)
    c: PointOnObject(g2,g1)
    c: Angle(g-1,g2) = 0.261799
    c: Coincident(g3,g0)
    c: Coincident(g4,g0)
    c: Angle(g-1,g3) = 0.19635
    c: Angle(g-1,g4) = 0.0654498
    c: Diameter(g5) = 43.2
    c: Parallel(g4,g7)
    c: Parallel(g6,g3)
    c: Distance(g6,g3) = 0.4
    c: Distance(g7,g4) = 0.4
    c: PointOnObject(g4,g1)
    c: PointOnObject(g3,g1)
    c: Coincident(g5,g6)
    c: Coincident(g5,g7)
    c: Coincident(g0,g5)
    c: Coincident(g8,g5)
    c: Coincident(g9,g5)
    c: Diameter(g9) = 48.4
    c: PointOnObject(g12,g2)
    c: Coincident(g10,g5)
    c: PointOnObject(g10,g-1)
    c: PointOnObject(g9,g10)
    c: Coincident(g11,g9)
    c: Parallel(g10,g11)
    c: Equal(g9,g12)
    c: Coincident(g9,g12)
    c: Coincident(g12,g6)
    c: Coincident(g9,g7)
    c: Coincident(g13,g12)
    c: Coincident(g13,g2)
    c: Coincident(g8,g13)
    c: Coincident(g11,g8)
FEATURE [PartDesign::Pocket] Pocket006
  BaseFeature = -> Revolution005
  Direction = (0,0,-1)
  Length = 15
  Length2 = 5
  Placement = pos=(0,0,0) rot=(1,0,0;1.5708rad)
  Profile = -> Sketch050
  ReferenceAxis = -> Sketch050 [N_Axis]
  Reversed = true
  Type = 0
  expr: Length = Spreadsheet.mmPulleyConnectorHeight
FEATURE [PartDesign::PolarPattern] PolarPattern004
  Angle = 360
  Axis = -> Sketch050 [N_Axis]
  BaseFeature = -> Pocket006
  Occurrences = 24
  Originals = -> [Pocket006]
  Placement = pos=(0,0,0) rot=(1,0,0;1.5708rad)
  expr: Angle = 360
  expr: Occurrences = Spreadsheet.cntPulleyConnectorTooth
FEATURE [PartDesign::Chamfer] Chamfer008
  Angle = 45
  Base = -> PolarPattern004 [Edge247,Edge237,Edge227,Edge257,Edge267,Edge277,Edge217,Edge207,Edge197,Edge187,Edge177,Edge167,Edge157,Edge147,Edge137,Edge367,Edge347,Edge357,Edge337,Edge287,Edge297,Edge307,Edge317,Edge327]
  BaseFeature = -> PolarPattern004
  ChamferType = 0
  FlipDirection = false
  Placement = pos=(0,0,0) rot=(1,0,0;1.5708rad)
  Size = 2.5
  Size2 = 1
  SupportTransform = false
  UseAllEdges = false
FEATURE [PartDesign::Body] Body013  label="PulleyBorderBody"
  Group = -> [Sketch049,Revolution005,Sketch050,Pocket006,PolarPattern004,Chamfer008]
  Origin = -> Origin025
  Tip = -> Chamfer008
COMPONENT P7 — recipe-attached ("PulleyOnAxisFixator", modeled in this document).
Construction recipe (the document's own serialized feature program — sketch geometry with constraints, then the solid features built on it; lengths are millimeters unless a unit is written):

FEATURE [Sketcher::SketchObject] Sketch054
  AttachmentOffset = pos=(0,0,-10.8) rot=(0,0,1;0rad)
  FullyConstrained = true
  MapMode = 5
  Placement = pos=(0,0,-10.8) rot=(0,0,1;0rad)
  Support = -> [XY_Plane025]
  expr: .AttachmentOffset.Base.z = -(Spreadsheet.mmPasWidth / 2 + Spreadsheet.mmPulleyConnectorThickness + Spreadsheet.mmAirSpace)
  expr: Constraints[2] = Spreadsheet.mmAxisTubeDia + Spreadsheet.mmPulleyConnectorThickness + Spreadsheet.mmAirSpace / 2
  expr: Constraints[3] = Spreadsheet.mmAxisTubeDia + Spreadsheet.mmPulleyConnectorThickness * 3
  sketch-geometry (2):
    g0: Circle CenterX=0 CenterY=0 CenterZ=0 NormalX=0 NormalY=0 NormalZ=1 AngleXU=0 Radius=22.6
    g1: Circle CenterX=0 CenterY=0 CenterZ=0 NormalX=0 NormalY=0 NormalZ=1 AngleXU=0 Radius=26.4
  constraints (4):
    c: Coincident(g0,g-1)
    c: Coincident(g1,g0)
    c: Diameter(g0) = 45.2
    c: Diameter(g1) = 52.8
FEATURE [PartDesign::Pad] Pad017
  Direction = (0,0,1)
  Length = 15
  Length2 = 10
  Profile = -> Sketch054
  ReferenceAxis = -> Sketch054 [N_Axis]
  Reversed = true
  Type = 0
  expr: Length = Spreadsheet.mmPulleyConnectorHeight
FEATURE [Sketcher::SketchObject] Sketch055
  AttachmentOffset = pos=(0,0,-25.8) rot=(0,0,1;0rad)
  FullyConstrained = false
  MapMode = 5
  Placement = pos=(0,0,-25.8) rot=(0,0,1;0rad)
  Support = -> [XY_Plane025]
  expr: .AttachmentOffset.Base.z = -(Spreadsheet.mmPulleyConnectorHeight + Spreadsheet.mmPasWidth / 2 + Spreadsheet.mmPulleyConnectorThickness + Spreadsheet.mmAirSpace)
  expr: Constraints[16] = Spreadsheet.mmAxisTubeDia + Spreadsheet.mmPulleyConnectorThickness - Spreadsheet.mmAirSpace / 2
  expr: Constraints[2] = Spreadsheet.mmAxisTubeDia
  expr: Constraints[32] = 360 / Spreadsheet.cntPulleyConnectorTooth / 4
  expr: Constraints[33] = 360 / Spreadsheet.cntPulleyConnectorTooth / 4
  expr: Constraints[34] = 360 / Spreadsheet.cntPulleyConnectorTooth / 2
  expr: Constraints[3] = Spreadsheet.mmAxisTubeDia + Spreadsheet.mmPulleyConnectorThickness * 2
  expr: Constraints[6] = Spreadsheet.mmAxisTubeDia + Spreadsheet.mmPulleyConnectorThickness
  sketch-geometry (15):
    g0: Circle CenterX=0 CenterY=0 CenterZ=0 NormalX=0 NormalY=0 NormalZ=1 AngleXU=0 Radius=20.4
    g1: Circle CenterX=0 CenterY=0 CenterZ=0 NormalX=0 NormalY=0 NormalZ=1 AngleXU=0 Radius=24.4
    g2: LineSegment StartX=0 StartY=0 StartZ=0 EndX=25.9633 EndY=3.41813 EndZ=0
    g3: LineSegment StartX=0 StartY=0 StartZ=0 EndX=24.7789 EndY=-3.2622 EndZ=0
    g4: ArcOfCircle CenterX=0 CenterY=0 CenterZ=0 NormalX=0 NormalY=0 NormalZ=1 AngleXU=0 Radius=22.4 StartAngle=6.15229 EndAngle=6.21774
    g5: LineSegment StartX=22.2084 StartY=2.92379 StartZ=0 EndX=22.0101 EndY=2.89768 EndZ=0
    g6: LineSegment StartX=22.0101 StartY=-2.89768 StartZ=0 EndX=22.2084 EndY=-2.92379 EndZ=0
    g7: ArcOfCircle CenterX=0 CenterY=0 CenterZ=0 NormalX=0 NormalY=0 NormalZ=1 AngleXU=0 Radius=22.2 StartAngle=6.15229 EndAngle=6.41409
    g8: LineSegment StartX=0 StartY=0 StartZ=0 EndX=26.0465 EndY=-1.70718 EndZ=0
    g9: LineSegment StartX=0 StartY=0 StartZ=0 EndX=26.0465 EndY=1.70718 EndZ=0
    g10: Circle CenterX=0 CenterY=0 CenterZ=0 NormalX=0 NormalY=0 NormalZ=1 AngleXU=0 Radius=22.2
    g11: ArcOfCircle CenterX=0 CenterY=0 CenterZ=0 NormalX=0 NormalY=0 NormalZ=1 AngleXU=0 Radius=22.4 StartAngle=0.0654498 EndAngle=0.1309
    g12: LineSegment StartX=22.352 StartY=1.46503 StartZ=0 EndX=24.3478 EndY=1.59584 EndZ=0
    g13: ArcOfCircle CenterX=0 CenterY=0 CenterZ=0 NormalX=0 NormalY=0 NormalZ=1 AngleXU=0 Radius=24.4 StartAngle=6.21774 EndAngle=6.34864
    g14: LineSegment StartX=22.352 StartY=-1.46503 StartZ=0 EndX=24.3478 EndY=-1.59584 EndZ=0
  constraints (38):
    c: Coincident(g0,g-1)
    c: Coincident(g1,g0)
    c: Diameter(g0) = 40.8
    c: Diameter(g1) = 48.8
    c: Coincident(g2,g0)
    c: Coincident(g3,g0)
    c: Diameter(g4) = 44.8
    c: Parallel(g3,g6)
    c: Parallel(g5,g2)
    c: Coincident(g11,g5)
    c: Coincident(g4,g6)
    c: Coincident(g0,g4)
    c: Coincident(g7,g4)
    c: Coincident(g8,g4)
    c: Coincident(g9,g4)
    c: Coincident(g10,g4)
    c: Diameter(g10) = 44.4
    c: Equal(g4,g11)
    c: PointOnObject(g4,g8)
    c: PointOnObject(g11,g9)
    c: Coincident(g4,g11)
    c: Coincident(g12,g11)
    c: PointOnObject(g5,g10)
    c: PointOnObject(g12,g1)
    c: Coincident(g14,g4)
    c: Parallel(g9,g12)
    c: PointOnObject(g5,g2)
    c: PointOnObject(g4,g3)
    c: Coincident(g13,g12)
    c: Coincident(g14,g13)
    c: Coincident(g7,g5)
    c: Coincident(g6,g7)
    c: Angle(g9,g2) = 0.0654498
    c: Angle(g3,g8) = 0.0654498
    c: Angle(g8,g9) = 0.1309
    c: Symmetric(g8,g9,g-1)
    c: Coincident(g4,g13)
    c: PointOnObject(g13,g8)
FEATURE [PartDesign::Pocket] Pocket009
  BaseFeature = -> Pad017
  Direction = (0,0,-1)
  Length = 15
  Length2 = 5
  Profile = -> Sketch055
  ReferenceAxis = -> Sketch055 [N_Axis]
  Reversed = true
  Type = 0
  expr: Length = Spreadsheet.mmPulleyConnectorHeight
FEATURE [PartDesign::PolarPattern] PolarPattern005
  Angle = 360
  Axis = -> Sketch055 [N_Axis]
  BaseFeature = -> Pocket009
  Occurrences = 24
  Originals = -> [Pocket009]
  expr: Occurrences = Spreadsheet.cntPulleyConnectorTooth
FEATURE [PartDesign::Chamfer] Chamfer006
  Angle = 45
  Base = -> PolarPattern005 [Edge2,Face2]
  BaseFeature = -> PolarPattern005
  ChamferType = 1
  FlipDirection = false
  Size = 0.3
  Size2 = 2
  SupportTransform = false
  UseAllEdges = false
FEATURE [Sketcher::SketchObject] Sketch056
  AttachmentOffset = pos=(0,0,-25.8) rot=(0,0,1;0rad)
  FullyConstrained = true
  MapMode = 5
  Placement = pos=(0,0,-25.8) rot=(0,0,1;0rad)
  Support = -> [XY_Plane025]
  expr: .AttachmentOffset.Base.z = -(Spreadsheet.mmPulleyConnectorHeight + Spreadsheet.mmPasWidth / 2 + Spreadsheet.mmPulleyConnectorThickness + Spreadsheet.mmAirSpace)
  expr: Constraints[2] = Spreadsheet.mmAxisTubeDia
  expr: Constraints[3] = Spreadsheet.mmAxisTubeDia + Spreadsheet.mmPetalHightMax * 4
  sketch-geometry (2):
    g0: Circle CenterX=0 CenterY=0 CenterZ=0 NormalX=0 NormalY=0 NormalZ=1 AngleXU=0 Radius=20.4
    g1: Circle CenterX=0 CenterY=0 CenterZ=0 NormalX=0 NormalY=0 NormalZ=1 AngleXU=0 Radius=32.64
  constraints (4):
    c: Coincident(g0,g-1)
    c: Coincident(g1,g0)
    c: Diameter(g0) = 40.8
    c: Diameter(g1) = 65.28
FEATURE [PartDesign::Pad] Pad018
  BaseFeature = -> Chamfer006
  Direction = (0,0,1)
  Length = 20.4
  Length2 = 10
  Profile = -> Sketch056
  ReferenceAxis = -> Sketch056 [N_Axis]
  Reversed = true
  Type = 0
  expr: Length = Spreadsheet.mmAxisTubeDia / 2
FEATURE [Sketcher::SketchObject] Sketch057  label="PulleyPetalPocketMaxSketch"
  AttachmentOffset = pos=(0,0,-46.2) rot=(0,0,1;0rad)
  FullyConstrained = true
  MapMode = 5
  Placement = pos=(0,0,-46.2) rot=(0,0,1;0rad)
  Support = -> [XY_Plane025]
  expr: .AttachmentOffset.Base.z = -(Spreadsheet.mmPulleyConnectorHeight + Spreadsheet.mmPasWidth / 2 + Spreadsheet.mmPulleyConnectorThickness + Spreadsheet.mmAirSpace + Spreadsheet.mmAxisTubeDia / 2)
  expr: Constraints[1] = Spreadsheet.mmAxisTubeDia
  expr: Constraints[7] = Spreadsheet.mmPetalPocketWidth
  expr: Constraints[8] = Spreadsheet.mmAxisTubeDia / 2 + Spreadsheet.mmPetalHightMax
  sketch-geometry (4):
    g0: ArcOfCircle CenterX=0 CenterY=0 CenterZ=0 NormalX=0 NormalY=0 NormalZ=1 AngleXU=0 Radius=20.4 StartAngle=6.00103 EndAngle=6.56534
    g1: LineSegment StartX=19.5933 StartY=5.67991 StartZ=0 EndX=26.52 EndY=5.67991 EndZ=0
    g2: LineSegment StartX=26.52 StartY=5.67991 StartZ=0 EndX=26.52 EndY=-5.67991 EndZ=0
    g3: LineSegment StartX=26.52 StartY=-5.67991 StartZ=0 EndX=19.5933 EndY=-5.67991 EndZ=0
  constraints (11):
    c: Coincident(g0,g-1)
    c: Diameter(g0) = 40.8
    c: Horizontal(g1)
    c: Coincident(g1,g2)
    c: Coincident(g2,g3)
    c: Horizontal(g3)
    c: Symmetric(g1,g2,g-1)
    c: DistanceY(g2,g2) = 11.3598
    c: DistanceX(g0,g2) = 26.52
    c: Coincident(g0,g1)
    c: Coincident(g0,g3)
FEATURE [Sketcher::SketchObject] Sketch058  label="PulleyPetalPocketMinSketch"
  AttachmentOffset = pos=(0,0,-27.84) rot=(0,0,1;0rad)
  FullyConstrained = true
  MapMode = 5
  Placement = pos=(0,0,-27.84) rot=(0,0,1;0rad)
  Support = -> [XY_Plane025]
  expr: .AttachmentOffset.Base.z = -(Spreadsheet.mmPulleyConnectorHeight + Spreadsheet.mmPasWidth / 2 + Spreadsheet.mmPulleyConnectorThickness + Spreadsheet.mmAirSpace + Spreadsheet.mmAxisTubeDia / 2 - Spreadsheet.mmFixatorHight * 0.9)
  expr: Constraints[1] = Spreadsheet.mmAxisTubeDia
  expr: Constraints[7] = Spreadsheet.mmAxisTubeDia / 2 + Spreadsheet.mmPetalHightMin
  expr: Constraints[8] = Spreadsheet.mmPetalPocketWidth
  sketch-geometry (4):
    g0: ArcOfCircle CenterX=0 CenterY=0 CenterZ=0 NormalX=0 NormalY=0 NormalZ=1 AngleXU=0 Radius=20.4 StartAngle=6.00103 EndAngle=6.56534
    g1: LineSegment StartX=19.5933 StartY=5.67991 StartZ=0 EndX=23.46 EndY=5.67991 EndZ=0
    g2: LineSegment StartX=23.46 StartY=5.67991 StartZ=0 EndX=23.46 EndY=-5.67991 EndZ=0
    g3: LineSegment StartX=23.46 StartY=-5.67991 StartZ=0 EndX=19.5933 EndY=-5.67991 EndZ=0
  constraints (11):
    c: Coincident(g0,g-1)
    c: Diameter(g0) = 40.8
    c: Horizontal(g1)
    c: Coincident(g1,g2)
    c: Coincident(g2,g3)
    c: Symmetric(g1,g2,g-1)
    c: Horizontal(g3)
    c: DistanceX(g0,g2) = 23.46
    c: DistanceY(g2,g2) = 11.3598
    c: Coincident(g0,g1)
    c: Coincident(g0,g3)
FEATURE [PartDesign::SubtractiveLoft] SubtractiveLoft003
  BaseFeature = -> Pad018
  Closed = false
  Profile = -> Sketch057
  Ruled = false
  Sections = -> [Sketch058]
FEATURE [PartDesign::PolarPattern] PolarPattern006
  Angle = 360
  Axis = -> Sketch057 [N_Axis]
  BaseFeature = -> SubtractiveLoft003
  Occurrences = 3
  Originals = -> [SubtractiveLoft003]
FEATURE [PartDesign::Fillet] Fillet002
  Base = -> PolarPattern006 [Edge2,Edge3,Edge4]
  BaseFeature = -> PolarPattern006
  Radius = 1
  SupportTransform = false
  UseAllEdges = false
FEATURE [PartDesign::Chamfer] Chamfer007
  Angle = 45
  Base = -> Fillet002 [Edge9,Edge17,Edge13]
  BaseFeature = -> Fillet002
  ChamferType = 0
  FlipDirection = false
  Size = 1
  Size2 = 1
  SupportTransform = false
  UseAllEdges = false
FEATURE [PartDesign::Body] Body015  label="PulleyOnAxisFixatorBody"
  Group = -> [Sketch054,Pad017,Sketch055,Pocket009,PolarPattern005,Chamfer006,Sketch056,Pad018,Sketch057,Sketch058,SubtractiveLoft003,PolarPattern006,Fillet002,Chamfer007]
  Origin = -> Origin029
  Tip = -> Chamfer007
COMPONENT P8 — recipe-attached ("PetalPart", modeled in this document).
Construction recipe (the document's own serialized feature program — sketch geometry with constraints, then the solid features built on it; lengths are millimeters unless a unit is written):

FEATURE [Sketcher::SketchObject] Sketch029  label="MaxPetalBase"
  FullyConstrained = false
  MapMode = 5
  Placement = pos=(0,0,0) rot=(0.57735,0.57735,0.57735;2.0944rad)
  Support = -> [YZ_Plane015]
  expr: Constraints[0] = Spreadsheet.mmAxisTubeDia + 2 * Spreadsheet.mmFixatorThick
  expr: Constraints[12] = Spreadsheet.mmAxisTubeDia / 2 + Spreadsheet.mmPetalHightMax
  expr: Constraints[16] = Spreadsheet.mmPetalWidth
  expr: Constraints[1] = Spreadsheet.mmAxisTubeDia
  expr: Constraints[6] = Spreadsheet.mmAxisTubeDia + Spreadsheet.mmTwoSideTapeThick * 2
  sketch-geometry (7):
    g0: Circle CenterX=0 CenterY=0 CenterZ=0 NormalX=0 NormalY=0 NormalZ=1 AngleXU=0 Radius=39.8652
    g1: Circle CenterX=0 CenterY=0 CenterZ=0 NormalX=0 NormalY=0 NormalZ=1 AngleXU=0 Radius=26.62
    g2: ArcOfCircle CenterX=0 CenterY=0 CenterZ=0 NormalX=0 NormalY=0 NormalZ=1 AngleXU=0 Radius=20.4 StartAngle=3.89684 EndAngle=6.80091
    g3: LineSegment StartX=19.8084 StartY=5.27991 StartZ=0 EndX=26.52 EndY=5.27991 EndZ=0
    g4: LineSegment StartX=26.52 StartY=5.27991 StartZ=0 EndX=26.52 EndY=-5.27991 EndZ=0
    g5: LineSegment StartX=26.52 StartY=-5.27991 StartZ=0 EndX=19.8084 EndY=-5.27991 EndZ=0
    g6: ArcOfCircle CenterX=0 CenterY=0 CenterZ=0 NormalX=0 NormalY=0 NormalZ=1 AngleXU=0 Radius=20.5 StartAngle=6.02269 EndAngle=6.54368
  constraints (20):
    c: Diameter(g1) = 53.24
    c: Diameter(g2) = 40.8
    c: Coincident(g3,g4)
    c: Coincident(g4,g5)
    c: PointOnObject(g3,g2)
    c: Coincident(g6,g0)
    c: Diameter(g6) = 41
    c: Coincident(g1,g6)
    c: Coincident(g0,g2)
    c: Vertical(g4)
    c: PointOnObject(g3,g6)
    c: PointOnObject(g5,g6)
    c: DistanceX(g-1,g4) = 26.52
    c: Horizontal(g3)
    c: Horizontal(g5)
    c: Symmetric(g5,g3,g-1)
    c: DistanceY(g5,g3) = 10.5598
    c: Coincident(g-1,g6)
    c: PointOnObject(g6,g5)
    c: PointOnObject(g6,g3)
FEATURE [Sketcher::SketchObject] Sketch030  label="MinPetalBase"
  AttachmentOffset = pos=(0,0,20.4) rot=(0,0,1;0rad)
  FullyConstrained = false
  MapMode = 5
  Placement = pos=(20.4,-4.5e-15,4.5e-15) rot=(0.57735,0.57735,0.57735;2.0944rad)
  Support = -> [YZ_Plane015]
  expr: .AttachmentOffset.Base.z = Spreadsheet.mmFixatorHight
  expr: Constraints[0] = Spreadsheet.mmAxisTubeDia + 2 * Spreadsheet.mmFixatorThick
  expr: Constraints[11] = Spreadsheet.mmAxisTubeDia / 2 + Spreadsheet.mmPetalHightMin
  expr: Constraints[15] = Spreadsheet.mmPetalWidth
  expr: Constraints[1] = Spreadsheet.mmAxisTubeDia
  expr: Constraints[5] = Spreadsheet.mmAxisTubeDia + Spreadsheet.mmTwoSideTapeThick * 2
  sketch-geometry (7):
    g0: Circle CenterX=0 CenterY=1.8e-15 CenterZ=0 NormalX=0 NormalY=0 NormalZ=1 AngleXU=0 Radius=39.865
    g1: Circle CenterX=0 CenterY=1.8e-15 CenterZ=0 NormalX=0 NormalY=0 NormalZ=1 AngleXU=0 Radius=26.62
    g2: ArcOfCircle CenterX=0 CenterY=1.8e-15 CenterZ=0 NormalX=0 NormalY=0 NormalZ=1 AngleXU=0 Radius=20.4 StartAngle=3.86544 EndAngle=6.7404
    g3: LineSegment StartX=19.8084 StartY=5.27991 StartZ=0 EndX=23.46 EndY=5.27991 EndZ=0
    g4: LineSegment StartX=23.46 StartY=5.27991 StartZ=0 EndX=23.46 EndY=-5.27991 EndZ=0
    g5: LineSegment StartX=23.46 StartY=-5.27991 StartZ=0 EndX=19.8084 EndY=-5.27991 EndZ=0
    g6: ArcOfCircle CenterX=0 CenterY=1.8e-15 CenterZ=0 NormalX=0 NormalY=0 NormalZ=1 AngleXU=0 Radius=20.5 StartAngle=6.02269 EndAngle=6.54368
  constraints (20):
    c: Diameter(g1) = 53.24
    c: Diameter(g2) = 40.8
    c: Coincident(g3,g4)
    c: Coincident(g4,g5)
    c: Coincident(g6,g0)
    c: Diameter(g6) = 41
    c: Coincident(g1,g6)
    c: Coincident(g0,g2)
    c: Vertical(g4)
    c: PointOnObject(g3,g6)
    c: PointOnObject(g5,g6)
    c: DistanceX(g-1,g4) = 23.46
    c: PointOnObject(g6,g5)
    c: PointOnObject(g6,g3)
    c: Coincident(g6,g-1)
    c: DistanceY(g5,g3) = 10.5598
    c: Symmetric(g5,g3,g-1)
    c: Horizontal(g3)
    c: Horizontal(g5)
    c: PointOnObject(g6,g-2)
FEATURE [PartDesign::AdditiveLoft] AdditiveLoft  label="PetalBodyBodyAdditiveLoft"
  Closed = false
  Placement = pos=(0,0,0) rot=(0.57735,0.57735,0.57735;2.0944rad)
  Profile = -> Sketch029
  Ruled = false
  Sections = -> [Sketch030]
FEATURE [PartDesign::Chamfer] Chamfer
  Angle = 45
  Base = -> AdditiveLoft [Edge8,Edge9,Edge6,Edge3,Edge2,Edge1,Edge11,Edge5]
  BaseFeature = -> AdditiveLoft
  ChamferType = 0
  FlipDirection = false
  Placement = pos=(0,0,0) rot=(0.57735,0.57735,0.57735;2.0944rad)
  Size = 1
  Size2 = 1
  SupportTransform = false
  UseAllEdges = false
FEATURE [PartDesign::Body] Body008  label="PetalBodyPart"
  Group = -> [Sketch029,Sketch030,AdditiveLoft,Chamfer]
  Origin = -> Origin015
  Tip = -> Chamfer
PROVENANCE & LICENSES
A FreeCAD (.FCStd) document from a public repository crawl; recipes are the document's own serialized feature recipes (and, for linked parts, companion documents' recipes).
License: as declared in the source repository (recorded in the dataset sidecar).
